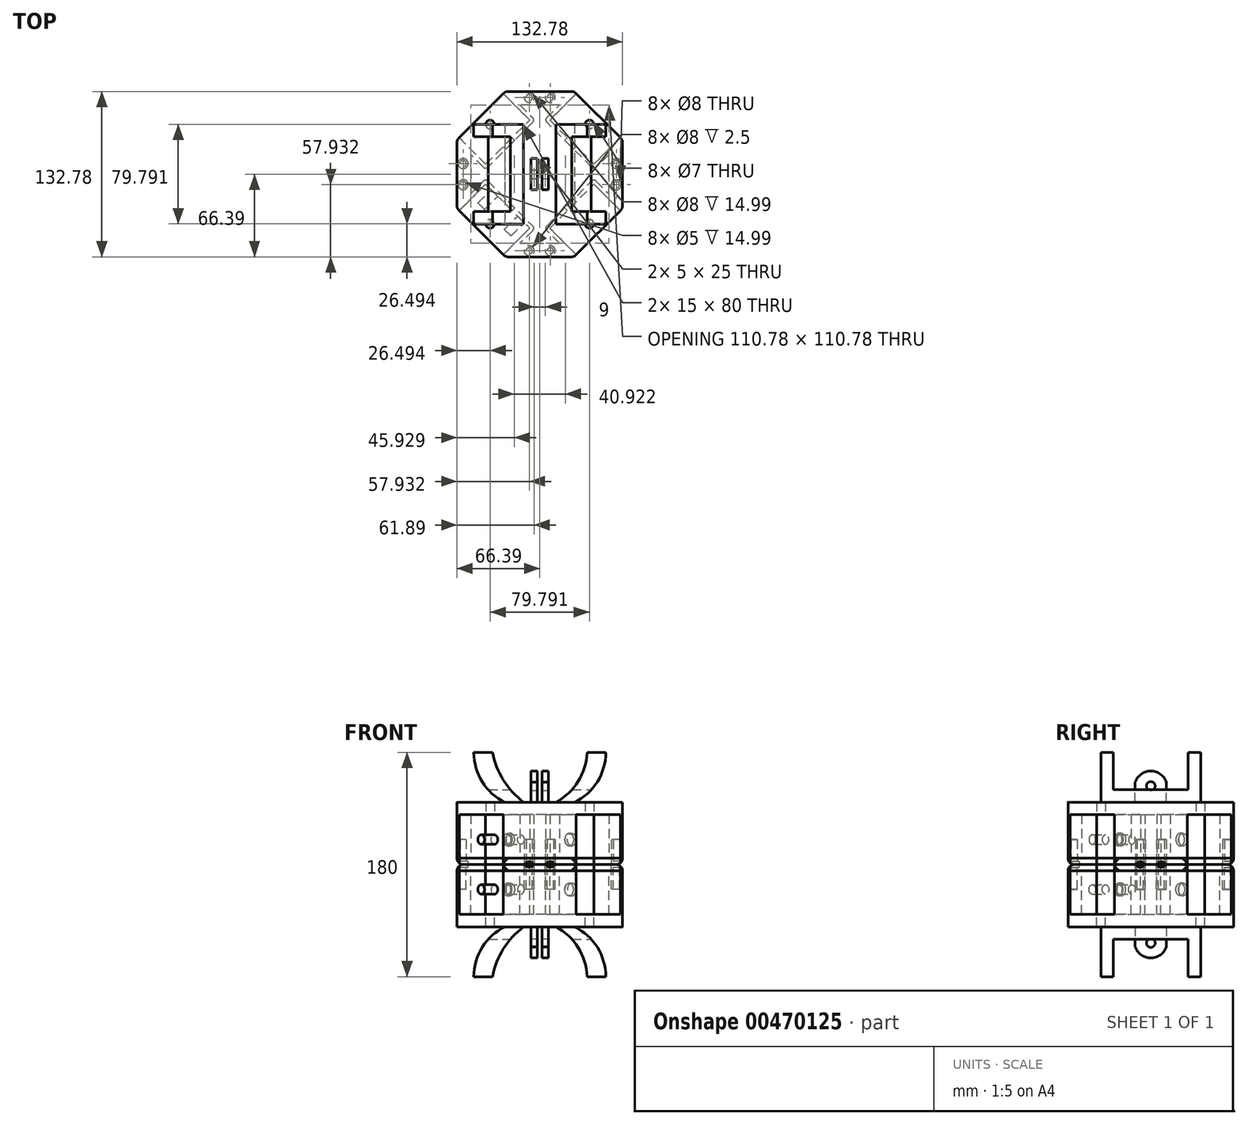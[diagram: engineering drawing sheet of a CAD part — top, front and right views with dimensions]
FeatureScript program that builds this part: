
annotation { "Feature Type Name" : "Feature", "Feature Type Description" : "" }
export const myFeature = defineFeature(function(context is Context, id is Id, definition is map)
    precondition{}
    {
        {
            var Q0;
            Q0=qCreatedBy(makeId("Top.planeOp"),FACE);
            var sketch = newSketch(context, id + "F0", { "sketchPlane" : qUnion([Q0])});
            skCircle(sketch, "E0.cCircle", {"center": v(0, 0) * mm, "radius": 71.86 * mm, "construction": true});
            skLineSegment(sketch, "E0.0", {"start": v(66.4, 27.5) * mm, "end": v(66.4, -27.5) * mm});
            skLineSegment(sketch, "E0.1", {"start": v(66.4, -27.5) * mm, "end": v(27.5, -66.4) * mm});
            skLineSegment(sketch, "E0.2", {"start": v(27.5, -66.4) * mm, "end": v(-27.5, -66.4) * mm});
            skLineSegment(sketch, "E0.3", {"start": v(-27.5, -66.4) * mm, "end": v(-66.4, -27.5) * mm});
            skLineSegment(sketch, "E0.4", {"start": v(-66.4, -27.5) * mm, "end": v(-66.4, 27.5) * mm});
            skLineSegment(sketch, "E0.5", {"start": v(-66.4, 27.5) * mm, "end": v(-27.5, 66.4) * mm});
            skLineSegment(sketch, "E0.6", {"start": v(-27.5, 66.4) * mm, "end": v(27.5, 66.4) * mm});
            skLineSegment(sketch, "E0.7", {"start": v(27.5, 66.4) * mm, "end": v(66.4, 27.5) * mm});
            skSolve(sketch);
        }
        {
            var Q0;
            Q0=makeQuery(id+"F0.imprint","IMPRINT",FACE,{"disambiguationData":[TD([[makeQuery(id+"F0.imprint","IMPRINT",EDGE,{"derivedFrom":sQuery(id+"F0.wireOp",EDGE,"E0.0")}),-1.0]])]});
            extrude(context, id + "F1", {"entities" : qUnion([Q0]), "depth" : 50 * mm});
        }
        {
            var Q0;
            Q0=makeQuery(id+"F1.opExtrude","CAP_FACE",FACE,{"disambiguationData":[OSD([sQuery(id+"F0.wireOp",EDGE,"E0.0"),sQuery(id+"F0.wireOp",EDGE,"E0.1"),sQuery(id+"F0.wireOp",EDGE,"E0.2"),sQuery(id+"F0.wireOp",EDGE,"E0.3"),sQuery(id+"F0.wireOp",EDGE,"E0.4"),sQuery(id+"F0.wireOp",EDGE,"E0.5"),sQuery(id+"F0.wireOp",EDGE,"E0.6"),sQuery(id+"F0.wireOp",EDGE,"E0.7")])],"isStart":true});
            var sketch = newSketch(context, id + "F2", { "sketchPlane" : qUnion([Q0])});
            skLineSegment(sketch, "E1", {"start": v(0, 66.4) * mm, "end": v(0, -66.4) * mm});
            skLineSegment(sketch, "E2.bottom", {"start": v(52.96, 40) * mm, "end": v(12.96, 40) * mm});
            skLineSegment(sketch, "E2.top", {"start": v(52.96, -40) * mm, "end": v(12.96, -40) * mm});
            skLineSegment(sketch, "E2.left", {"start": v(52.96, 40) * mm, "end": v(52.96, -40) * mm});
            skLineSegment(sketch, "E2.right", {"start": v(12.96, 40) * mm, "end": v(12.96, -40) * mm});
            skPoint(sketch, "E2.middle", {"position": v(32.96, 0) * mm});
            skLineSegment(sketch, "E3.MirrorCS", {"start": v(-12.96, 40) * mm, "end": v(-12.96, -40) * mm});
            skLineSegment(sketch, "E4.MirrorCS", {"start": v(-52.96, 40) * mm, "end": v(-12.96, 40) * mm});
            skLineSegment(sketch, "E5.MirrorCS", {"start": v(-52.96, 40) * mm, "end": v(-52.96, -40) * mm});
            skLineSegment(sketch, "E6.MirrorCS", {"start": v(-52.96, -40) * mm, "end": v(-12.96, -40) * mm});
            skSolve(sketch);
        }
        {
            var Q0;
            Q0 = qSketchRegion(id + "F2", true);
            extrude(context, id + "F3", {"entities" : qUnion([Q0]), "operationType" : NewBodyOperationType.ADD, "depth" : 40 * mm});
        }
        {
            var Q0;
            Q0=makeQuery(id+"F3.opExtrude","SWEPT_FACE",FACE,{"disambiguationData":[OSD([sQuery(id+"F2.wireOp",EDGE,"E2.bottom")])]});
            var sketch = newSketch(context, id + "F4", { "sketchPlane" : qUnion([Q0])});
            skArc(sketch, "E7", {"start": v(52.96, -40) * mm, "mid": v(46.2, -16.42) * mm, "end": v(27.96, 0) * mm});
            skArc(sketch, "E8", {"start": v(37.96, -40) * mm, "mid": v(30.79, -16.67) * mm, "end": v(12.96, 0) * mm});
            skLineSegment(sketch, "E9", {"start": v(0, 0) * mm, "end": v(0, -51.15) * mm});
            skArc(sketch, "E10.MirrorCS", {"start": v(-37.96, -40) * mm, "mid": v(-30.79, -16.67) * mm, "end": v(-12.96, 0) * mm});
            skArc(sketch, "E11.MirrorCS", {"start": v(-52.96, -40) * mm, "mid": v(-46.2, -16.42) * mm, "end": v(-27.96, 0) * mm});
            skLineSegment(sketch, "E12", {"start": v(-37.96, -40) * mm, "end": v(-52.96, -40) * mm});
            skLineSegment(sketch, "E13", {"start": v(-27.96, 0) * mm, "end": v(-12.96, 0) * mm});
            skSolve(sketch);
        }
        {
            var Q0;
            {var subQ0=sQuery(id+"F4.wireOp",EDGE,"E7");Q0=makeQuery(id+"F4.imprint","IMPRINT",FACE,{"disambiguationData":[TD([[makeQuery(id+"F4.imprint","IMPRINT",EDGE,{"derivedFrom":subQ0}),-1.0]])]});}
            var Q1;
            {var subQ0=sQuery(id+"F4.wireOp",EDGE,"E8");Q1=makeQuery(id+"F4.imprint","IMPRINT",FACE,{"disambiguationData":[TD([[makeQuery(id+"F4.imprint","IMPRINT",EDGE,{"derivedFrom":subQ0}),1.0]])]});}
            extrude(context, id + "F5", {"entities" : qUnion([Q0, Q1]), "operationType" : NewBodyOperationType.REMOVE, "endBound" : BoundingType.THROUGH_ALL, "oppositeDirection" : true, "depth" : 25 * mm});
        }
        {
            var Q0;
            Q0=makeQuery(id+"F3.opExtrude","SWEPT_FACE",FACE,{"disambiguationData":[OSD([sQuery(id+"F2.wireOp",EDGE,"E4.MirrorCS")])]});
            var sketch = newSketch(context, id + "F6", { "sketchPlane" : qUnion([Q0])});
            skArc(sketch, "E14", {"start": v(-27.96, 0) * mm, "mid": v(-46.2, -16.42) * mm, "end": v(-52.96, -40) * mm});
            skArc(sketch, "E15", {"start": v(-12.96, 0) * mm, "mid": v(-29.15, -17.7) * mm, "end": v(-37.96, -40) * mm});
            skSolve(sketch);
        }
        {
            var Q0;
            {var subQ0=sQuery(id+"F6.wireOp",EDGE,"E15");Q0=makeQuery(id+"F6.imprint","IMPRINT",FACE,{"disambiguationData":[TD([[makeQuery(id+"F6.imprint","IMPRINT",EDGE,{"derivedFrom":subQ0}),1.0]])]});}
            var Q1;
            {var subQ0=sQuery(id+"F6.wireOp",EDGE,"E14");Q1=makeQuery(id+"F6.imprint","IMPRINT",FACE,{"disambiguationData":[TD([[makeQuery(id+"F6.imprint","IMPRINT",EDGE,{"derivedFrom":subQ0}),-1.0]])]});}
            extrude(context, id + "F7", {"entities" : qUnion([Q0, Q1]), "operationType" : NewBodyOperationType.REMOVE, "endBound" : BoundingType.THROUGH_ALL, "oppositeDirection" : true, "depth" : 25 * mm});
        }
        {
            var Q0;
            Q0=makeQuery(id+"F3.opExtrude","CAP_FACE",FACE,{"disambiguationData":[OSD([sQuery(id+"F2.wireOp",EDGE,"E2.bottom"),sQuery(id+"F2.wireOp",EDGE,"E2.top"),sQuery(id+"F2.wireOp",EDGE,"E2.left"),sQuery(id+"F2.wireOp",EDGE,"E2.right")])],"isStart":false});
            extrude(context, id + "F8", {"entities" : qUnion([Q0]), "operationType" : NewBodyOperationType.ADD, "depth" : 10 * mm});
        }
        {
            var Q0;
            Q0=makeQuery(id+"F8.opExtrude","SWEPT_FACE",FACE,{"disambiguationData":[OSD([sQuery(id+"F2.wireOp",EDGE,"E2.bottom"),sQuery(id+"F2.wireOp",EDGE,"E2.left"),sQuery(id+"F4.wireOp",EDGE,"E7")])]});
            var sketch = newSketch(context, id + "F9", { "sketchPlane" : qUnion([Q0])});
            skLineSegment(sketch, "E16.bottom", {"start": v(-30, -50) * mm, "end": v(30, -50) * mm});
            skLineSegment(sketch, "E16.top", {"start": v(-30, -10) * mm, "end": v(30, -10) * mm});
            skLineSegment(sketch, "E16.left", {"start": v(-30, -50) * mm, "end": v(-30, -10) * mm});
            skLineSegment(sketch, "E16.right", {"start": v(30, -50) * mm, "end": v(30, -10) * mm});
            skLineSegment(sketch, "E17.bottom", {"start": v(-40, -40) * mm, "end": v(40, -40) * mm});
            skLineSegment(sketch, "E17.top", {"start": v(-40, -50) * mm, "end": v(40, -50) * mm});
            skLineSegment(sketch, "E17.left", {"start": v(-40, -40) * mm, "end": v(-40, -50) * mm});
            skLineSegment(sketch, "E17.right", {"start": v(40, -40) * mm, "end": v(40, -50) * mm});
            skSolve(sketch);
        }
        {
            var Q0;
            Q0 = qSketchRegion(id + "F9", true);
            extrude(context, id + "F10", {"entities" : qUnion([Q0]), "operationType" : NewBodyOperationType.REMOVE, "endBound" : BoundingType.THROUGH_ALL, "oppositeDirection" : true, "depth" : 25 * mm});
        }
        {
            var Q0;
            Q0=makeQuery(id+"F1.opExtrude","CAP_FACE",FACE,{"disambiguationData":[OSD([sQuery(id+"F0.wireOp",EDGE,"E0.0"),sQuery(id+"F0.wireOp",EDGE,"E0.1"),sQuery(id+"F0.wireOp",EDGE,"E0.2"),sQuery(id+"F0.wireOp",EDGE,"E0.3"),sQuery(id+"F0.wireOp",EDGE,"E0.4"),sQuery(id+"F0.wireOp",EDGE,"E0.5"),sQuery(id+"F0.wireOp",EDGE,"E0.6"),sQuery(id+"F0.wireOp",EDGE,"E0.7")])],"isStart":false});
            var sketch = newSketch(context, id + "F11", { "sketchPlane" : qUnion([Q0])});
            skLineSegment(sketch, "E18", {"start": v(29.27, -64.62) * mm, "end": v(8.05, -43.4) * mm});
            skLineSegment(sketch, "E19", {"start": v(64.62, -29.27) * mm, "end": v(43.4, -8.05) * mm});
            skLineSegment(sketch, "E20", {"start": v(8.05, -43.4) * mm, "end": v(43.4, -8.05) * mm});
            skLineSegment(sketch, "E21", {"start": v(43.4, 43.4) * mm, "end": v(-46.95, -46.95) * mm});
            skLineSegment(sketch, "E22", {"start": v(46.95, -46.95) * mm, "end": v(-46.95, 46.95) * mm});
            skLineSegment(sketch, "E23", {"start": v(-29.27, -64.62) * mm, "end": v(-8.05, -43.4) * mm});
            skLineSegment(sketch, "E24", {"start": v(-64.62, -29.27) * mm, "end": v(-43.4, -8.05) * mm});
            skLineSegment(sketch, "E25", {"start": v(-43.4, -8.05) * mm, "end": v(-8.05, -43.4) * mm});
            skLineSegment(sketch, "E26.MirrorCS", {"start": v(29.27, 64.62) * mm, "end": v(8.05, 43.4) * mm});
            skLineSegment(sketch, "E27.MirrorCS", {"start": v(8.05, 43.4) * mm, "end": v(43.4, 8.05) * mm});
            skLineSegment(sketch, "E28.MirrorCS", {"start": v(64.62, 29.27) * mm, "end": v(43.4, 8.05) * mm});
            skLineSegment(sketch, "E29.MirrorCS", {"start": v(-43.4, 8.05) * mm, "end": v(-8.05, 43.4) * mm});
            skLineSegment(sketch, "E30.MirrorCS", {"start": v(-29.27, 64.62) * mm, "end": v(-8.05, 43.4) * mm});
            skLineSegment(sketch, "E31", {"start": v(-43.4, 8.05) * mm, "end": v(-64.62, 29.27) * mm});
            skSolve(sketch);
        }
        {
            var Q0;
            {var subQ5=sQuery(id+"F11.wireOp",EDGE,"0e1623ae-2a34-4fe9-b9fa-2a8e952514210.MirrorCS");Q0=makeQuery(id+"F11.imprint","IMPRINT",FACE,{"disambiguationData":[TD([[makeQuery(id+"F11.imprint","IMPRINT",EDGE,{"derivedFrom":subQ5}),1.0]])]});}
            var Q1;
            {var subQ5=sQuery(id+"F11.wireOp",EDGE,"E30.MirrorCS");Q1=makeQuery(id+"F11.imprint","IMPRINT",FACE,{"disambiguationData":[TD([[makeQuery(id+"F11.imprint","IMPRINT",EDGE,{"derivedFrom":subQ5}),-1.0]])]});}
            var Q2;
            {var subQ5=sQuery(id+"F11.wireOp",EDGE,"E26.MirrorCS");Q2=makeQuery(id+"F11.imprint","IMPRINT",FACE,{"disambiguationData":[TD([[makeQuery(id+"F11.imprint","IMPRINT",EDGE,{"derivedFrom":subQ5}),1.0]])]});}
            var Q3;
            {var subQ5=sQuery(id+"F11.wireOp",EDGE,"E28.MirrorCS");Q3=makeQuery(id+"F11.imprint","IMPRINT",FACE,{"disambiguationData":[TD([[makeQuery(id+"F11.imprint","IMPRINT",EDGE,{"derivedFrom":subQ5}),-1.0]])]});}
            var Q4;
            {var subQ0=sQuery(id+"F11.wireOp",EDGE,"E19");Q4=makeQuery(id+"F11.imprint","IMPRINT",FACE,{"disambiguationData":[TD([[makeQuery(id+"F11.imprint","IMPRINT",EDGE,{"derivedFrom":subQ0}),1.0]])]});}
            var Q5;
            {var subQ0=sQuery(id+"F11.wireOp",EDGE,"E18");Q5=makeQuery(id+"F11.imprint","IMPRINT",FACE,{"disambiguationData":[TD([[makeQuery(id+"F11.imprint","IMPRINT",EDGE,{"derivedFrom":subQ0}),-1.0]])]});}
            var Q6;
            {var subQ5=sQuery(id+"F11.wireOp",EDGE,"E24");Q6=makeQuery(id+"F11.imprint","IMPRINT",FACE,{"disambiguationData":[TD([[makeQuery(id+"F11.imprint","IMPRINT",EDGE,{"derivedFrom":subQ5}),-1.0]])]});}
            var Q7;
            {var subQ5=sQuery(id+"F11.wireOp",EDGE,"E23");Q7=makeQuery(id+"F11.imprint","IMPRINT",FACE,{"disambiguationData":[TD([[makeQuery(id+"F11.imprint","IMPRINT",EDGE,{"derivedFrom":subQ5}),1.0]])]});}
            var Q8;
            {var subQ5=sQuery(id+"F11.wireOp",EDGE,"E31");Q8=makeQuery(id+"F11.imprint","IMPRINT",FACE,{"disambiguationData":[TD([[makeQuery(id+"F11.imprint","IMPRINT",EDGE,{"derivedFrom":subQ5}),-1.0]])]});}
            extrude(context, id + "F12", {"entities" : qUnion([Q0, Q1, Q2, Q3, Q4, Q5, Q6, Q7, Q8]), "operationType" : NewBodyOperationType.REMOVE, "oppositeDirection" : true, "depth" : 40 * mm});
        }
        {
            var Q0;
            {var subQ0=sQuery(id+"F2.wireOp",EDGE,"E4.MirrorCS");var subQ1=makeQuery(id+"F3.opExtrude","CAP_EDGE",EDGE,{"disambiguationData":[OSD([subQ0])],"isStart":true});var subQ2=sQuery(id+"F2.wireOp",EDGE,"E2.bottom");var subQ3=makeQuery(id+"F3.opExtrude","CAP_EDGE",EDGE,{"disambiguationData":[OSD([subQ2])],"isStart":true});Q0=makeQuery(id+"F7.boolean.opBoolean","MERGE",FACE,{"derivedFrom":[makeQuery(id+"F5.boolean.opBoolean","MERGE",FACE,{"derivedFrom":[makeQuery(id+"F1.opExtrude","CAP_FACE",FACE,{"disambiguationData":[OSD([sQuery(id+"F0.wireOp",EDGE,"E0.0"),sQuery(id+"F0.wireOp",EDGE,"E0.1"),sQuery(id+"F0.wireOp",EDGE,"E0.2"),sQuery(id+"F0.wireOp",EDGE,"E0.3"),sQuery(id+"F0.wireOp",EDGE,"E0.4"),sQuery(id+"F0.wireOp",EDGE,"E0.5"),sQuery(id+"F0.wireOp",EDGE,"E0.6"),sQuery(id+"F0.wireOp",EDGE,"E0.7")])],"isStart":true}),makeQuery(id+"F5.opExtrude","SWEPT_FACE",FACE,{"disambiguationData":[OSD([subQ2]),TDD([makeQuery(id+"F4.imprint","IMPRINT",EDGE,{"disambiguationData":[TD([[makeQuery(id+"F4.imprint","INTERSECT",VERTEX,{"derivedFrom":[subQ3,sQuery(id+"F4.wireOp",EDGE,"E7")]}),1.0]])],"derivedFrom":subQ3})])]})]}),makeQuery(id+"F7.opExtrude","SWEPT_FACE",FACE,{"disambiguationData":[OSD([subQ0]),TDD([makeQuery(id+"F6.imprint","IMPRINT",EDGE,{"disambiguationData":[TD([[makeQuery(id+"F6.imprint","INTERSECT",VERTEX,{"derivedFrom":[subQ1,sQuery(id+"F6.wireOp",EDGE,"E14")]}),1.0]])],"derivedFrom":subQ1})])]})]});}
            var sketch = newSketch(context, id + "F13", { "sketchPlane" : qUnion([Q0])});
            skLineSegment(sketch, "E32.bottom", {"start": v(10, 12.5) * mm, "end": v(-10, 12.5) * mm});
            skLineSegment(sketch, "E32.top", {"start": v(10, -12.5) * mm, "end": v(-10, -12.5) * mm});
            skLineSegment(sketch, "E32.left", {"start": v(10, 12.5) * mm, "end": v(10, -12.5) * mm});
            skLineSegment(sketch, "E32.right", {"start": v(-10, 12.5) * mm, "end": v(-10, -12.5) * mm});
            skPoint(sketch, "E32.middle", {"position": v(0, 0) * mm});
            skSolve(sketch);
        }
        {
            var Q0;
            Q0 = qSketchRegion(id + "F13", true);
            extrude(context, id + "F14", {"entities" : qUnion([Q0]), "operationType" : NewBodyOperationType.ADD, "depth" : 25 * mm});
        }
        {
            var Q0;
            Q0=makeQuery(id+"F14.opExtrude","CAP_FACE",FACE,{"disambiguationData":[OSD([sQuery(id+"F13.wireOp",EDGE,"E32.bottom"),sQuery(id+"F13.wireOp",EDGE,"E32.top"),sQuery(id+"F13.wireOp",EDGE,"E32.left"),sQuery(id+"F13.wireOp",EDGE,"E32.right")])],"isStart":false});
            var sketch = newSketch(context, id + "F15", { "sketchPlane" : qUnion([Q0])});
            skLineSegment(sketch, "E33.bottom", {"start": v(-7, 12.5) * mm, "end": v(-2, 12.5) * mm});
            skLineSegment(sketch, "E33.top", {"start": v(-7, -12.5) * mm, "end": v(-2, -12.5) * mm});
            skLineSegment(sketch, "E33.left", {"start": v(-7, 12.5) * mm, "end": v(-7, -12.5) * mm});
            skLineSegment(sketch, "E33.right", {"start": v(-2, 12.5) * mm, "end": v(-2, -12.5) * mm});
            skLineSegment(sketch, "E34.bottom", {"start": v(7, 12.5) * mm, "end": v(2, 12.5) * mm});
            skLineSegment(sketch, "E34.top", {"start": v(7, -12.5) * mm, "end": v(2, -12.5) * mm});
            skLineSegment(sketch, "E34.left", {"start": v(7, 12.5) * mm, "end": v(7, -12.5) * mm});
            skLineSegment(sketch, "E34.right", {"start": v(2, 12.5) * mm, "end": v(2, -12.5) * mm});
            skSolve(sketch);
        }
        {
            var Q0;
            Q0=makeQuery(id+"F14.opExtrude","SWEPT_FACE",FACE,{"disambiguationData":[OSD([sQuery(id+"F13.wireOp",EDGE,"E32.left")])]});
            var sketch = newSketch(context, id + "F16", { "sketchPlane" : qUnion([Q0])});
            skPoint(sketch, "E35", {"position": v(0, -25) * mm});
            skPoint(sketch, "E36", {"position": v(12.5, -16.09) * mm});
            skPoint(sketch, "E37", {"position": v(-12.5, -16.09) * mm});
            skArc(sketch, "E38", {"start": v(-12.5, -16.09) * mm, "mid": v(0, -25) * mm, "end": v(12.5, -16.09) * mm});
            skCircle(sketch, "E39", {"center": v(0, -13) * mm, "radius": 3.5 * mm});
            skSolve(sketch);
        }
        {
            var Q0;
            {var subQ0=sQuery(id+"F16.wireOp",EDGE,"E38");var subQ1=sQuery(id+"F13.wireOp",EDGE,"E32.left");var subQ4=makeQuery(id+"F14.opExtrude","CAP_EDGE",EDGE,{"disambiguationData":[OSD([subQ1])],"isStart":false});var subQ5=makeQuery(id+"F16.imprint","INTERSECT",VERTEX,{"derivedFrom":[subQ4,subQ0]});Q0=makeQuery(id+"F16.imprint","IMPRINT",FACE,{"disambiguationData":[TD([[makeQuery(id+"F16.imprint","IMPRINT",EDGE,{"disambiguationData":[TD([[subQ5,-1.0]])],"derivedFrom":subQ0}),-1.0]])]});}
            var Q1;
            {var subQ0=sQuery(id+"F16.wireOp",EDGE,"E38");var subQ1=sQuery(id+"F13.wireOp",EDGE,"E32.left");var subQ4=makeQuery(id+"F14.opExtrude","CAP_EDGE",EDGE,{"disambiguationData":[OSD([subQ1])],"isStart":false});var subQ5=makeQuery(id+"F16.imprint","INTERSECT",VERTEX,{"derivedFrom":[subQ4,subQ0]});Q1=makeQuery(id+"F16.imprint","IMPRINT",FACE,{"disambiguationData":[TD([[makeQuery(id+"F16.imprint","IMPRINT",EDGE,{"disambiguationData":[TD([[subQ5,1.0]])],"derivedFrom":subQ0}),-1.0]])]});}
            extrude(context, id + "F17", {"entities" : qUnion([Q0, Q1]), "operationType" : NewBodyOperationType.REMOVE, "endBound" : BoundingType.THROUGH_ALL, "oppositeDirection" : true, "depth" : 25 * mm});
        }
        {
            var Q0;
            {var subQ0=sQuery(id+"F15.wireOp",EDGE,"E34.left");Q0=makeQuery(id+"F15.imprint","IMPRINT",FACE,{"disambiguationData":[TD([[makeQuery(id+"F15.imprint","IMPRINT",EDGE,{"derivedFrom":subQ0}),1.0]])]});}
            var Q1;
            {var subQ0=sQuery(id+"F15.wireOp",EDGE,"E33.right");Q1=makeQuery(id+"F15.imprint","IMPRINT",FACE,{"disambiguationData":[TD([[makeQuery(id+"F15.imprint","IMPRINT",EDGE,{"derivedFrom":subQ0}),1.0]])]});}
            var Q2;
            {var subQ0=sQuery(id+"F15.wireOp",EDGE,"E33.left");Q2=makeQuery(id+"F15.imprint","IMPRINT",FACE,{"disambiguationData":[TD([[makeQuery(id+"F15.imprint","IMPRINT",EDGE,{"derivedFrom":subQ0}),-1.0]])]});}
            extrude(context, id + "F18", {"entities" : qUnion([Q0, Q1, Q2]), "operationType" : NewBodyOperationType.REMOVE, "oppositeDirection" : true, "depth" : 25 * mm});
        }
        {
            var Q0;
            Q0=makeQuery(id+"F12.boolean.opBoolean","COPY",FACE,{"derivedFrom":makeQuery(id+"F12.opExtrude","CAP_FACE",FACE,{"disambiguationData":[OSD([sQuery(id+"F0.wireOp",EDGE,"E0.1"),sQuery(id+"F11.wireOp",EDGE,"E18"),sQuery(id+"F11.wireOp",EDGE,"E19"),sQuery(id+"F11.wireOp",EDGE,"E20")])],"isStart":false})});
            var sketch = newSketch(context, id + "F19", { "sketchPlane" : qUnion([Q0])});
            skCircle(sketch, "E40", {"center": v(39.9, -39.85) * mm, "radius": 3.5 * mm});
            skSolve(sketch);
        }
        {
            var Q0;
            Q0 = qSketchRegion(id + "F16", true);
            extrude(context, id + "F20", {"entities" : qUnion([Q0]), "operationType" : NewBodyOperationType.REMOVE, "oppositeDirection" : true, "depth" : 25 * mm});
        }
        {
            var Q0;
            Q0=makeQuery(id+"F12.boolean.opBoolean","COPY",FACE,{"derivedFrom":makeQuery(id+"F12.opExtrude","CAP_FACE",FACE,{"disambiguationData":[OSD([sQuery(id+"F0.wireOp",EDGE,"E0.3"),sQuery(id+"F11.wireOp",EDGE,"E23"),sQuery(id+"F11.wireOp",EDGE,"E24"),sQuery(id+"F11.wireOp",EDGE,"E25")])],"isStart":false})});
            var sketch = newSketch(context, id + "F21", { "sketchPlane" : qUnion([Q0])});
            skCircle(sketch, "E41", {"center": v(-39.85, -39.9) * mm, "radius": 3.5 * mm});
            skSolve(sketch);
        }
        {
            var Q0;
            Q0=makeQuery(id+"F12.boolean.opBoolean","COPY",FACE,{"derivedFrom":makeQuery(id+"F12.opExtrude","CAP_FACE",FACE,{"disambiguationData":[OSD([sQuery(id+"F0.wireOp",EDGE,"E0.5"),sQuery(id+"F11.wireOp",EDGE,"E29.MirrorCS"),sQuery(id+"F11.wireOp",EDGE,"0e1623ae-2a34-4fe9-b9fa-2a8e952514210.MirrorCS"),sQuery(id+"F11.wireOp",EDGE,"E30.MirrorCS")])],"isStart":false})});
            var sketch = newSketch(context, id + "F22", { "sketchPlane" : qUnion([Q0])});
            skCircle(sketch, "E42", {"center": v(-39.9, 39.85) * mm, "radius": 3.5 * mm});
            skSolve(sketch);
        }
        {
            var Q0;
            Q0=makeQuery(id+"F12.boolean.opBoolean","COPY",FACE,{"derivedFrom":makeQuery(id+"F12.opExtrude","CAP_FACE",FACE,{"disambiguationData":[OSD([sQuery(id+"F0.wireOp",EDGE,"E0.7"),sQuery(id+"F11.wireOp",EDGE,"E26.MirrorCS"),sQuery(id+"F11.wireOp",EDGE,"E27.MirrorCS"),sQuery(id+"F11.wireOp",EDGE,"E28.MirrorCS")])],"isStart":false})});
            var sketch = newSketch(context, id + "F23", { "sketchPlane" : qUnion([Q0])});
            skCircle(sketch, "E43", {"center": v(39.85, 39.9) * mm, "radius": 3.5 * mm});
            skSolve(sketch);
        }
        {
            var Q0;
            Q0=makeQuery(id+"F22.imprint","IMPRINT",FACE,{"disambiguationData":[TD([[makeQuery(id+"F22.imprint","IMPRINT",EDGE,{"derivedFrom":sQuery(id+"F22.wireOp",EDGE,"E42")}),1.0]])]});
            var Q1;
            Q1=makeQuery(id+"F23.imprint","IMPRINT",FACE,{"disambiguationData":[TD([[makeQuery(id+"F23.imprint","IMPRINT",EDGE,{"derivedFrom":sQuery(id+"F23.wireOp",EDGE,"E43")}),1.0]])]});
            var Q2;
            Q2=makeQuery(id+"F19.imprint","IMPRINT",FACE,{"disambiguationData":[TD([[makeQuery(id+"F19.imprint","IMPRINT",EDGE,{"derivedFrom":sQuery(id+"F19.wireOp",EDGE,"E40")}),1.0]])]});
            var Q3;
            Q3=makeQuery(id+"F21.imprint","IMPRINT",FACE,{"disambiguationData":[TD([[makeQuery(id+"F21.imprint","IMPRINT",EDGE,{"derivedFrom":sQuery(id+"F21.wireOp",EDGE,"E41")}),1.0]])]});
            extrude(context, id + "F24", {"entities" : qUnion([Q0, Q1, Q2, Q3]), "operationType" : NewBodyOperationType.REMOVE, "oppositeDirection" : true, "depth" : 10 * mm});
        }
        {
            var Q0;
            Q0=makeQuery(id+"F1.opExtrude","CAP_EDGE",EDGE,{"disambiguationData":[OSD([sQuery(id+"F0.wireOp",EDGE,"E0.2")])],"isStart":false});
            var Q1;
            Q1=makeQuery(id+"F1.opExtrude","CAP_EDGE",EDGE,{"disambiguationData":[OSD([sQuery(id+"F0.wireOp",EDGE,"E0.0")])],"isStart":false});
            var Q2;
            Q2=makeQuery(id+"F1.opExtrude","CAP_EDGE",EDGE,{"disambiguationData":[OSD([sQuery(id+"F0.wireOp",EDGE,"E0.6")])],"isStart":false});
            var Q3;
            Q3=makeQuery(id+"F1.opExtrude","CAP_EDGE",EDGE,{"disambiguationData":[OSD([sQuery(id+"F0.wireOp",EDGE,"E0.4")])],"isStart":false});
            var Q4;
            Q4=makeQuery(id+"F1.opExtrude","SWEPT_EDGE",EDGE,{"disambiguationData":[OSD([sQuery(id+"F0.wireOp",EDGE,"E0.1"),sQuery(id+"F0.wireOp",EDGE,"E0.2")])]});
            var Q5;
            Q5=makeQuery(id+"F1.opExtrude","SWEPT_EDGE",EDGE,{"disambiguationData":[OSD([sQuery(id+"F0.wireOp",EDGE,"E0.2"),sQuery(id+"F0.wireOp",EDGE,"E0.3")])]});
            var Q6;
            Q6=makeQuery(id+"F1.opExtrude","SWEPT_EDGE",EDGE,{"disambiguationData":[OSD([sQuery(id+"F0.wireOp",EDGE,"E0.0"),sQuery(id+"F0.wireOp",EDGE,"E0.1")])]});
            var Q7;
            Q7=makeQuery(id+"F1.opExtrude","SWEPT_EDGE",EDGE,{"disambiguationData":[OSD([sQuery(id+"F0.wireOp",EDGE,"E0.0"),sQuery(id+"F0.wireOp",EDGE,"E0.7")])]});
            var Q8;
            Q8=makeQuery(id+"F1.opExtrude","SWEPT_EDGE",EDGE,{"disambiguationData":[OSD([sQuery(id+"F0.wireOp",EDGE,"E0.6"),sQuery(id+"F0.wireOp",EDGE,"E0.7")])]});
            var Q9;
            Q9=makeQuery(id+"F1.opExtrude","SWEPT_EDGE",EDGE,{"disambiguationData":[OSD([sQuery(id+"F0.wireOp",EDGE,"E0.4"),sQuery(id+"F0.wireOp",EDGE,"E0.5")])]});
            var Q10;
            Q10=makeQuery(id+"F1.opExtrude","SWEPT_EDGE",EDGE,{"disambiguationData":[OSD([sQuery(id+"F0.wireOp",EDGE,"E0.3"),sQuery(id+"F0.wireOp",EDGE,"E0.4")])]});
            var Q11;
            Q11=makeQuery(id+"F1.opExtrude","SWEPT_EDGE",EDGE,{"disambiguationData":[OSD([sQuery(id+"F0.wireOp",EDGE,"E0.5"),sQuery(id+"F0.wireOp",EDGE,"E0.6")])]});
            fillet(context, id + "F25", {"entities" : qUnion([Q0, Q1, Q2, Q3, Q4, Q5, Q6, Q7, Q8, Q9, Q10, Q11]), "radius" : 5 * mm, "tangentPropagation" : true, "allowEdgeOverflow" : false});
        }
        {
            var Q0;
            Q0=makeQuery(id+"F1.opExtrude","SWEPT_FACE",FACE,{"disambiguationData":[OSD([sQuery(id+"F0.wireOp",EDGE,"E0.2")])]});
            var sketch = newSketch(context, id + "F26", { "sketchPlane" : qUnion([Q0])});
            skLineSegment(sketch, "E44.bottom", {"start": v(90.93, 45) * mm, "end": v(-90.93, 45) * mm});
            skLineSegment(sketch, "E44.top", {"start": v(90.93, 44.99) * mm, "end": v(-90.93, 44.99) * mm});
            skLineSegment(sketch, "E44.left", {"start": v(90.93, 45) * mm, "end": v(90.93, 44.99) * mm});
            skLineSegment(sketch, "E44.right", {"start": v(-90.93, 45) * mm, "end": v(-90.93, 44.99) * mm});
            skPoint(sketch, "E44.middle", {"position": v(0, 45) * mm});
            skPoint(sketch, "E44.middle.positionSnap0", {"position": v(0, 45) * mm});
            skPoint(sketch, "E44.cornerSnap0", {"position": v(0, 45) * mm});
            skPoint(sketch, "E44.centerSnap0", {"position": v(0, 45) * mm});
            skSolve(sketch);
        }
        {
            var Q0;
            Q0 = qSketchRegion(id + "F26", true);
            extrude(context, id + "F27", {"entities" : qUnion([Q0]), "operationType" : NewBodyOperationType.REMOVE, "endBound" : BoundingType.THROUGH_ALL, "oppositeDirection" : true, "depth" : 25 * mm});
        }
        {
            var Q0;
            Q0=makeQuery(id+"F27.boolean.opBoolean","COPY",FACE,{"derivedFrom":makeQuery(id+"F27.opExtrude","SWEPT_FACE",FACE,{"disambiguationData":[OSD([sQuery(id+"F26.wireOp",EDGE,"E44.top")])]})});
            var sketch = newSketch(context, id + "F28", { "sketchPlane" : qUnion([Q0])});
            skLineSegment(sketch, "E45.0", {"start": v(-3.81, -43.4) * mm, "end": v(-23.8, -63.4) * mm});
            skLineSegment(sketch, "E45.1", {"start": v(-43.4, -3.81) * mm, "end": v(-3.81, -43.4) * mm});
            skLineSegment(sketch, "E45.2", {"start": v(-63.4, -23.8) * mm, "end": v(-43.4, -3.81) * mm});
            skLineSegment(sketch, "E45.3", {"start": v(-63.4, 23.8) * mm, "end": v(-63.4, -23.8) * mm});
            skLineSegment(sketch, "E45.4", {"start": v(-43.4, 3.81) * mm, "end": v(-63.4, 23.8) * mm});
            skLineSegment(sketch, "E45.5", {"start": v(63.4, -23.8) * mm, "end": v(63.4, 23.8) * mm});
            skLineSegment(sketch, "E45.6", {"start": v(43.4, -3.81) * mm, "end": v(63.4, -23.8) * mm});
            skLineSegment(sketch, "E45.7", {"start": v(3.81, -43.4) * mm, "end": v(43.4, -3.81) * mm});
            skLineSegment(sketch, "E45.8", {"start": v(23.8, -63.4) * mm, "end": v(3.81, -43.4) * mm});
            skLineSegment(sketch, "E45.9", {"start": v(63.4, 23.8) * mm, "end": v(43.4, 3.81) * mm});
            skLineSegment(sketch, "E45.10", {"start": v(43.4, 3.81) * mm, "end": v(3.81, 43.4) * mm});
            skLineSegment(sketch, "E45.11", {"start": v(3.81, 43.4) * mm, "end": v(23.8, 63.4) * mm});
            skLineSegment(sketch, "E45.12", {"start": v(23.8, 63.4) * mm, "end": v(-23.8, 63.4) * mm});
            skLineSegment(sketch, "E45.13", {"start": v(-23.8, 63.4) * mm, "end": v(-3.81, 43.4) * mm});
            skLineSegment(sketch, "E45.14", {"start": v(-23.8, -63.4) * mm, "end": v(23.8, -63.4) * mm});
            skLineSegment(sketch, "E45.15", {"start": v(-3.81, 43.4) * mm, "end": v(-43.4, 3.81) * mm});
            skLineSegment(sketch, "E46.0", {"start": v(15.8, 55.4) * mm, "end": v(-15.8, 55.4) * mm});
            skLineSegment(sketch, "E47.0", {"start": v(-55.4, 15.8) * mm, "end": v(-55.4, -15.8) * mm});
            skLineSegment(sketch, "E48.0", {"start": v(-15.8, -55.4) * mm, "end": v(15.8, -55.4) * mm});
            skLineSegment(sketch, "E49.0", {"start": v(55.4, -15.8) * mm, "end": v(55.4, 15.8) * mm});
            skSolve(sketch);
        }
        {
            var Q0;
            {var subQ1=sQuery(id+"F11.wireOp",EDGE,"E20");Q0=makeQuery(id+"F27.boolean.opBoolean","SPLIT",FACE,{"disambiguationData":[TD([makeQuery(id+"F27.opExtrude","SWEPT_FACE",FACE,{"disambiguationData":[OSD([sQuery(id+"F26.wireOp",EDGE,"E44.top")])]})])],"derivedFrom":makeQuery(id+"F12.boolean.opBoolean","COPY",FACE,{"derivedFrom":makeQuery(id+"F12.opExtrude","SWEPT_FACE",FACE,{"disambiguationData":[OSD([subQ1])]})})});}
            var sketch = newSketch(context, id + "F29", { "sketchPlane" : qUnion([Q0])});
            skCircle(sketch, "E50", {"center": v(0, 30) * mm, "radius": 5 * mm});
            skPoint(sketch, "E50.centerSnap0", {"position": v(0, 10) * mm});
            skSolve(sketch);
        }
        {
            var Q0;
            Q0 = qSketchRegion(id + "F29", true);
            extrude(context, id + "F30", {"entities" : qUnion([Q0]), "operationType" : NewBodyOperationType.REMOVE, "endBound" : BoundingType.THROUGH_ALL, "oppositeDirection" : true, "depth" : 25 * mm});
        }
        {
            var Q0;
            {var subQ1=sQuery(id+"F11.wireOp",EDGE,"E25");Q0=makeQuery(id+"F27.boolean.opBoolean","SPLIT",FACE,{"disambiguationData":[TD([makeQuery(id+"F27.opExtrude","SWEPT_FACE",FACE,{"disambiguationData":[OSD([sQuery(id+"F26.wireOp",EDGE,"E44.top")])]})])],"derivedFrom":makeQuery(id+"F12.boolean.opBoolean","COPY",FACE,{"derivedFrom":makeQuery(id+"F12.opExtrude","SWEPT_FACE",FACE,{"disambiguationData":[OSD([subQ1])]})})});}
            var sketch = newSketch(context, id + "F31", { "sketchPlane" : qUnion([Q0])});
            skCircle(sketch, "E51", {"center": v(0, 30) * mm, "radius": 5 * mm});
            skPoint(sketch, "E51.centerSnap0", {"position": v(0, 10) * mm});
            skCircle(sketch, "E52", {"center": v(15, 30) * mm, "radius": 3.75 * mm});
            skCircle(sketch, "E53", {"center": v(-15, 30) * mm, "radius": 3.75 * mm});
            skSolve(sketch);
        }
        {
            var Q0;
            Q0=makeQuery(id+"F31.imprint","IMPRINT",FACE,{"disambiguationData":[TD([[makeQuery(id+"F31.imprint","IMPRINT",EDGE,{"derivedFrom":sQuery(id+"F31.wireOp",EDGE,"E51")}),1.0]])]});
            extrude(context, id + "F32", {"entities" : qUnion([Q0]), "operationType" : NewBodyOperationType.REMOVE, "endBound" : BoundingType.THROUGH_ALL, "oppositeDirection" : true, "depth" : 25 * mm});
        }
        {
            var Q0;
            Q0=makeQuery(id+"F1.opExtrude","CAP_FACE",FACE,{"disambiguationData":[OSD([sQuery(id+"F0.wireOp",EDGE,"E0.0"),sQuery(id+"F0.wireOp",EDGE,"E0.1"),sQuery(id+"F0.wireOp",EDGE,"E0.2"),sQuery(id+"F0.wireOp",EDGE,"E0.3"),sQuery(id+"F0.wireOp",EDGE,"E0.4"),sQuery(id+"F0.wireOp",EDGE,"E0.5"),sQuery(id+"F0.wireOp",EDGE,"E0.6"),sQuery(id+"F0.wireOp",EDGE,"E0.7")])],"isStart":false});
            var sketch = newSketch(context, id + "F33", { "sketchPlane" : qUnion([Q0])});
            skCircle(sketch, "E54", {"center": v(-8.46, -61.5) * mm, "radius": 2.5 * mm});
            skCircle(sketch, "E55", {"center": v(8.46, -61.5) * mm, "radius": 2.5 * mm});
            skCircle(sketch, "E56.MirrorC", {"center": v(-8.46, 61.5) * mm, "radius": 2.5 * mm});
            skCircle(sketch, "E57.MirrorC", {"center": v(8.46, 61.5) * mm, "radius": 2.5 * mm});
            skCircle(sketch, "E58", {"center": v(-61.5, 8.46) * mm, "radius": 2.5 * mm});
            skCircle(sketch, "E59", {"center": v(-61.5, -8.46) * mm, "radius": 2.5 * mm});
            skCircle(sketch, "E60.MirrorC", {"center": v(61.5, 8.46) * mm, "radius": 2.5 * mm});
            skCircle(sketch, "E61.MirrorC", {"center": v(61.5, -8.46) * mm, "radius": 2.5 * mm});
            skCircle(sketch, "E62", {"center": v(-61.5, 8.46) * mm, "radius": 4 * mm});
            skCircle(sketch, "E63", {"center": v(-61.5, -8.46) * mm, "radius": 4 * mm});
            skCircle(sketch, "E64", {"center": v(-8.46, -61.5) * mm, "radius": 4 * mm});
            skCircle(sketch, "E65", {"center": v(8.46, -61.5) * mm, "radius": 4 * mm});
            skCircle(sketch, "E66", {"center": v(61.5, -8.46) * mm, "radius": 4 * mm});
            skCircle(sketch, "E67", {"center": v(61.5, 8.46) * mm, "radius": 4 * mm});
            skCircle(sketch, "E68", {"center": v(8.46, 61.5) * mm, "radius": 4 * mm});
            skCircle(sketch, "E69", {"center": v(-8.46, 61.5) * mm, "radius": 4 * mm});
            skSolve(sketch);
        }
        {
            var Q0;
            {var subQ0=sQuery(id+"F33.wireOp",EDGE,"E56.MirrorC");var subQ1=sQuery(id+"F0.wireOp",EDGE,"E0.6");var subQ2=makeQuery(id+"F25.opFillet","BLEND_EDGE",EDGE,{"blendedFrom":[makeQuery(id+"F1.opExtrude","CAP_EDGE",EDGE,{"disambiguationData":[OSD([subQ1])],"isStart":false}),makeQuery(id+"F1.opExtrude","CAP_FACE",FACE,{"disambiguationData":[OSD([sQuery(id+"F0.wireOp",EDGE,"E0.0"),sQuery(id+"F0.wireOp",EDGE,"E0.1"),sQuery(id+"F0.wireOp",EDGE,"E0.2"),sQuery(id+"F0.wireOp",EDGE,"E0.3"),sQuery(id+"F0.wireOp",EDGE,"E0.4"),sQuery(id+"F0.wireOp",EDGE,"E0.5"),subQ1,sQuery(id+"F0.wireOp",EDGE,"E0.7")])],"isStart":false})],"blendedInto":[makeQuery(id+"F1.opExtrude","CAP_FACE",FACE,{"disambiguationData":[OSD([sQuery(id+"F0.wireOp",EDGE,"E0.0"),sQuery(id+"F0.wireOp",EDGE,"E0.1"),sQuery(id+"F0.wireOp",EDGE,"E0.2"),sQuery(id+"F0.wireOp",EDGE,"E0.3"),sQuery(id+"F0.wireOp",EDGE,"E0.4"),sQuery(id+"F0.wireOp",EDGE,"E0.5"),subQ1,sQuery(id+"F0.wireOp",EDGE,"E0.7")])],"isStart":false})]});var subQ3=makeQuery(id+"F33.imprint","INTERSECT",VERTEX,{"disambiguationData":[OD(0.0)],"derivedFrom":[subQ2,subQ0]});Q0=makeQuery(id+"F33.imprint","IMPRINT",FACE,{"disambiguationData":[TD([[makeQuery(id+"F33.imprint","IMPRINT",EDGE,{"disambiguationData":[TD([[subQ3,-1.0]])],"derivedFrom":subQ0}),-1.0]])]});}
            var Q1;
            {var subQ0=sQuery(id+"F33.wireOp",EDGE,"E56.MirrorC");var subQ1=sQuery(id+"F0.wireOp",EDGE,"E0.6");var subQ2=makeQuery(id+"F25.opFillet","BLEND_EDGE",EDGE,{"blendedFrom":[makeQuery(id+"F1.opExtrude","CAP_EDGE",EDGE,{"disambiguationData":[OSD([subQ1])],"isStart":false}),makeQuery(id+"F1.opExtrude","CAP_FACE",FACE,{"disambiguationData":[OSD([sQuery(id+"F0.wireOp",EDGE,"E0.0"),sQuery(id+"F0.wireOp",EDGE,"E0.1"),sQuery(id+"F0.wireOp",EDGE,"E0.2"),sQuery(id+"F0.wireOp",EDGE,"E0.3"),sQuery(id+"F0.wireOp",EDGE,"E0.4"),sQuery(id+"F0.wireOp",EDGE,"E0.5"),subQ1,sQuery(id+"F0.wireOp",EDGE,"E0.7")])],"isStart":false})],"blendedInto":[makeQuery(id+"F1.opExtrude","CAP_FACE",FACE,{"disambiguationData":[OSD([sQuery(id+"F0.wireOp",EDGE,"E0.0"),sQuery(id+"F0.wireOp",EDGE,"E0.1"),sQuery(id+"F0.wireOp",EDGE,"E0.2"),sQuery(id+"F0.wireOp",EDGE,"E0.3"),sQuery(id+"F0.wireOp",EDGE,"E0.4"),sQuery(id+"F0.wireOp",EDGE,"E0.5"),subQ1,sQuery(id+"F0.wireOp",EDGE,"E0.7")])],"isStart":false})]});var subQ3=makeQuery(id+"F33.imprint","INTERSECT",VERTEX,{"disambiguationData":[OD(0.0)],"derivedFrom":[subQ2,subQ0]});Q1=makeQuery(id+"F33.imprint","IMPRINT",FACE,{"disambiguationData":[TD([[makeQuery(id+"F33.imprint","IMPRINT",EDGE,{"disambiguationData":[TD([[subQ3,1.0]])],"derivedFrom":subQ0}),-1.0]])]});}
            var Q2;
            {var subQ0=sQuery(id+"F33.wireOp",EDGE,"E57.MirrorC");var subQ1=sQuery(id+"F0.wireOp",EDGE,"E0.6");var subQ2=makeQuery(id+"F25.opFillet","BLEND_EDGE",EDGE,{"blendedFrom":[makeQuery(id+"F1.opExtrude","CAP_EDGE",EDGE,{"disambiguationData":[OSD([subQ1])],"isStart":false}),makeQuery(id+"F1.opExtrude","CAP_FACE",FACE,{"disambiguationData":[OSD([sQuery(id+"F0.wireOp",EDGE,"E0.0"),sQuery(id+"F0.wireOp",EDGE,"E0.1"),sQuery(id+"F0.wireOp",EDGE,"E0.2"),sQuery(id+"F0.wireOp",EDGE,"E0.3"),sQuery(id+"F0.wireOp",EDGE,"E0.4"),sQuery(id+"F0.wireOp",EDGE,"E0.5"),subQ1,sQuery(id+"F0.wireOp",EDGE,"E0.7")])],"isStart":false})],"blendedInto":[makeQuery(id+"F1.opExtrude","CAP_FACE",FACE,{"disambiguationData":[OSD([sQuery(id+"F0.wireOp",EDGE,"E0.0"),sQuery(id+"F0.wireOp",EDGE,"E0.1"),sQuery(id+"F0.wireOp",EDGE,"E0.2"),sQuery(id+"F0.wireOp",EDGE,"E0.3"),sQuery(id+"F0.wireOp",EDGE,"E0.4"),sQuery(id+"F0.wireOp",EDGE,"E0.5"),subQ1,sQuery(id+"F0.wireOp",EDGE,"E0.7")])],"isStart":false})]});var subQ3=makeQuery(id+"F33.imprint","INTERSECT",VERTEX,{"disambiguationData":[OD(0.0)],"derivedFrom":[subQ2,subQ0]});Q2=makeQuery(id+"F33.imprint","IMPRINT",FACE,{"disambiguationData":[TD([[makeQuery(id+"F33.imprint","IMPRINT",EDGE,{"disambiguationData":[TD([[subQ3,1.0]])],"derivedFrom":subQ0}),-1.0]])]});}
            var Q3;
            {var subQ0=sQuery(id+"F33.wireOp",EDGE,"E57.MirrorC");var subQ1=sQuery(id+"F0.wireOp",EDGE,"E0.6");var subQ2=makeQuery(id+"F25.opFillet","BLEND_EDGE",EDGE,{"blendedFrom":[makeQuery(id+"F1.opExtrude","CAP_EDGE",EDGE,{"disambiguationData":[OSD([subQ1])],"isStart":false}),makeQuery(id+"F1.opExtrude","CAP_FACE",FACE,{"disambiguationData":[OSD([sQuery(id+"F0.wireOp",EDGE,"E0.0"),sQuery(id+"F0.wireOp",EDGE,"E0.1"),sQuery(id+"F0.wireOp",EDGE,"E0.2"),sQuery(id+"F0.wireOp",EDGE,"E0.3"),sQuery(id+"F0.wireOp",EDGE,"E0.4"),sQuery(id+"F0.wireOp",EDGE,"E0.5"),subQ1,sQuery(id+"F0.wireOp",EDGE,"E0.7")])],"isStart":false})],"blendedInto":[makeQuery(id+"F1.opExtrude","CAP_FACE",FACE,{"disambiguationData":[OSD([sQuery(id+"F0.wireOp",EDGE,"E0.0"),sQuery(id+"F0.wireOp",EDGE,"E0.1"),sQuery(id+"F0.wireOp",EDGE,"E0.2"),sQuery(id+"F0.wireOp",EDGE,"E0.3"),sQuery(id+"F0.wireOp",EDGE,"E0.4"),sQuery(id+"F0.wireOp",EDGE,"E0.5"),subQ1,sQuery(id+"F0.wireOp",EDGE,"E0.7")])],"isStart":false})]});var subQ3=makeQuery(id+"F33.imprint","INTERSECT",VERTEX,{"disambiguationData":[OD(0.0)],"derivedFrom":[subQ2,subQ0]});Q3=makeQuery(id+"F33.imprint","IMPRINT",FACE,{"disambiguationData":[TD([[makeQuery(id+"F33.imprint","IMPRINT",EDGE,{"disambiguationData":[TD([[subQ3,-1.0]])],"derivedFrom":subQ0}),-1.0]])]});}
            var Q4;
            {var subQ0=sQuery(id+"F33.wireOp",EDGE,"E58");var subQ1=sQuery(id+"F0.wireOp",EDGE,"E0.4");var subQ2=makeQuery(id+"F25.opFillet","BLEND_EDGE",EDGE,{"blendedFrom":[makeQuery(id+"F1.opExtrude","CAP_EDGE",EDGE,{"disambiguationData":[OSD([subQ1])],"isStart":false}),makeQuery(id+"F1.opExtrude","CAP_FACE",FACE,{"disambiguationData":[OSD([sQuery(id+"F0.wireOp",EDGE,"E0.0"),sQuery(id+"F0.wireOp",EDGE,"E0.1"),sQuery(id+"F0.wireOp",EDGE,"E0.2"),sQuery(id+"F0.wireOp",EDGE,"E0.3"),subQ1,sQuery(id+"F0.wireOp",EDGE,"E0.5"),sQuery(id+"F0.wireOp",EDGE,"E0.6"),sQuery(id+"F0.wireOp",EDGE,"E0.7")])],"isStart":false})],"blendedInto":[makeQuery(id+"F1.opExtrude","CAP_FACE",FACE,{"disambiguationData":[OSD([sQuery(id+"F0.wireOp",EDGE,"E0.0"),sQuery(id+"F0.wireOp",EDGE,"E0.1"),sQuery(id+"F0.wireOp",EDGE,"E0.2"),sQuery(id+"F0.wireOp",EDGE,"E0.3"),subQ1,sQuery(id+"F0.wireOp",EDGE,"E0.5"),sQuery(id+"F0.wireOp",EDGE,"E0.6"),sQuery(id+"F0.wireOp",EDGE,"E0.7")])],"isStart":false})]});var subQ3=makeQuery(id+"F33.imprint","INTERSECT",VERTEX,{"disambiguationData":[OD(0.0)],"derivedFrom":[subQ2,subQ0]});Q4=makeQuery(id+"F33.imprint","IMPRINT",FACE,{"disambiguationData":[TD([[makeQuery(id+"F33.imprint","IMPRINT",EDGE,{"disambiguationData":[TD([[subQ3,-1.0]])],"derivedFrom":subQ0}),1.0]])]});}
            var Q5;
            {var subQ0=sQuery(id+"F33.wireOp",EDGE,"E58");var subQ1=sQuery(id+"F0.wireOp",EDGE,"E0.4");var subQ2=makeQuery(id+"F25.opFillet","BLEND_EDGE",EDGE,{"blendedFrom":[makeQuery(id+"F1.opExtrude","CAP_EDGE",EDGE,{"disambiguationData":[OSD([subQ1])],"isStart":false}),makeQuery(id+"F1.opExtrude","CAP_FACE",FACE,{"disambiguationData":[OSD([sQuery(id+"F0.wireOp",EDGE,"E0.0"),sQuery(id+"F0.wireOp",EDGE,"E0.1"),sQuery(id+"F0.wireOp",EDGE,"E0.2"),sQuery(id+"F0.wireOp",EDGE,"E0.3"),subQ1,sQuery(id+"F0.wireOp",EDGE,"E0.5"),sQuery(id+"F0.wireOp",EDGE,"E0.6"),sQuery(id+"F0.wireOp",EDGE,"E0.7")])],"isStart":false})],"blendedInto":[makeQuery(id+"F1.opExtrude","CAP_FACE",FACE,{"disambiguationData":[OSD([sQuery(id+"F0.wireOp",EDGE,"E0.0"),sQuery(id+"F0.wireOp",EDGE,"E0.1"),sQuery(id+"F0.wireOp",EDGE,"E0.2"),sQuery(id+"F0.wireOp",EDGE,"E0.3"),subQ1,sQuery(id+"F0.wireOp",EDGE,"E0.5"),sQuery(id+"F0.wireOp",EDGE,"E0.6"),sQuery(id+"F0.wireOp",EDGE,"E0.7")])],"isStart":false})]});var subQ3=makeQuery(id+"F33.imprint","INTERSECT",VERTEX,{"disambiguationData":[OD(0.0)],"derivedFrom":[subQ2,subQ0]});Q5=makeQuery(id+"F33.imprint","IMPRINT",FACE,{"disambiguationData":[TD([[makeQuery(id+"F33.imprint","IMPRINT",EDGE,{"disambiguationData":[TD([[subQ3,1.0]])],"derivedFrom":subQ0}),1.0]])]});}
            var Q6;
            {var subQ0=sQuery(id+"F33.wireOp",EDGE,"E59");var subQ1=sQuery(id+"F0.wireOp",EDGE,"E0.4");var subQ2=makeQuery(id+"F25.opFillet","BLEND_EDGE",EDGE,{"blendedFrom":[makeQuery(id+"F1.opExtrude","CAP_EDGE",EDGE,{"disambiguationData":[OSD([subQ1])],"isStart":false}),makeQuery(id+"F1.opExtrude","CAP_FACE",FACE,{"disambiguationData":[OSD([sQuery(id+"F0.wireOp",EDGE,"E0.0"),sQuery(id+"F0.wireOp",EDGE,"E0.1"),sQuery(id+"F0.wireOp",EDGE,"E0.2"),sQuery(id+"F0.wireOp",EDGE,"E0.3"),subQ1,sQuery(id+"F0.wireOp",EDGE,"E0.5"),sQuery(id+"F0.wireOp",EDGE,"E0.6"),sQuery(id+"F0.wireOp",EDGE,"E0.7")])],"isStart":false})],"blendedInto":[makeQuery(id+"F1.opExtrude","CAP_FACE",FACE,{"disambiguationData":[OSD([sQuery(id+"F0.wireOp",EDGE,"E0.0"),sQuery(id+"F0.wireOp",EDGE,"E0.1"),sQuery(id+"F0.wireOp",EDGE,"E0.2"),sQuery(id+"F0.wireOp",EDGE,"E0.3"),subQ1,sQuery(id+"F0.wireOp",EDGE,"E0.5"),sQuery(id+"F0.wireOp",EDGE,"E0.6"),sQuery(id+"F0.wireOp",EDGE,"E0.7")])],"isStart":false})]});var subQ3=makeQuery(id+"F33.imprint","INTERSECT",VERTEX,{"disambiguationData":[OD(0.0)],"derivedFrom":[subQ2,subQ0]});Q6=makeQuery(id+"F33.imprint","IMPRINT",FACE,{"disambiguationData":[TD([[makeQuery(id+"F33.imprint","IMPRINT",EDGE,{"disambiguationData":[TD([[subQ3,1.0]])],"derivedFrom":subQ0}),1.0]])]});}
            var Q7;
            {var subQ0=sQuery(id+"F33.wireOp",EDGE,"E59");var subQ1=sQuery(id+"F0.wireOp",EDGE,"E0.4");var subQ2=makeQuery(id+"F25.opFillet","BLEND_EDGE",EDGE,{"blendedFrom":[makeQuery(id+"F1.opExtrude","CAP_EDGE",EDGE,{"disambiguationData":[OSD([subQ1])],"isStart":false}),makeQuery(id+"F1.opExtrude","CAP_FACE",FACE,{"disambiguationData":[OSD([sQuery(id+"F0.wireOp",EDGE,"E0.0"),sQuery(id+"F0.wireOp",EDGE,"E0.1"),sQuery(id+"F0.wireOp",EDGE,"E0.2"),sQuery(id+"F0.wireOp",EDGE,"E0.3"),subQ1,sQuery(id+"F0.wireOp",EDGE,"E0.5"),sQuery(id+"F0.wireOp",EDGE,"E0.6"),sQuery(id+"F0.wireOp",EDGE,"E0.7")])],"isStart":false})],"blendedInto":[makeQuery(id+"F1.opExtrude","CAP_FACE",FACE,{"disambiguationData":[OSD([sQuery(id+"F0.wireOp",EDGE,"E0.0"),sQuery(id+"F0.wireOp",EDGE,"E0.1"),sQuery(id+"F0.wireOp",EDGE,"E0.2"),sQuery(id+"F0.wireOp",EDGE,"E0.3"),subQ1,sQuery(id+"F0.wireOp",EDGE,"E0.5"),sQuery(id+"F0.wireOp",EDGE,"E0.6"),sQuery(id+"F0.wireOp",EDGE,"E0.7")])],"isStart":false})]});var subQ3=makeQuery(id+"F33.imprint","INTERSECT",VERTEX,{"disambiguationData":[OD(0.0)],"derivedFrom":[subQ2,subQ0]});Q7=makeQuery(id+"F33.imprint","IMPRINT",FACE,{"disambiguationData":[TD([[makeQuery(id+"F33.imprint","IMPRINT",EDGE,{"disambiguationData":[TD([[subQ3,-1.0]])],"derivedFrom":subQ0}),1.0]])]});}
            var Q8;
            {var subQ0=sQuery(id+"F33.wireOp",EDGE,"E61.MirrorC");var subQ1=sQuery(id+"F0.wireOp",EDGE,"E0.0");var subQ2=makeQuery(id+"F25.opFillet","BLEND_EDGE",EDGE,{"blendedFrom":[makeQuery(id+"F1.opExtrude","CAP_EDGE",EDGE,{"disambiguationData":[OSD([subQ1])],"isStart":false}),makeQuery(id+"F1.opExtrude","CAP_FACE",FACE,{"disambiguationData":[OSD([subQ1,sQuery(id+"F0.wireOp",EDGE,"E0.1"),sQuery(id+"F0.wireOp",EDGE,"E0.2"),sQuery(id+"F0.wireOp",EDGE,"E0.3"),sQuery(id+"F0.wireOp",EDGE,"E0.4"),sQuery(id+"F0.wireOp",EDGE,"E0.5"),sQuery(id+"F0.wireOp",EDGE,"E0.6"),sQuery(id+"F0.wireOp",EDGE,"E0.7")])],"isStart":false})],"blendedInto":[makeQuery(id+"F1.opExtrude","CAP_FACE",FACE,{"disambiguationData":[OSD([subQ1,sQuery(id+"F0.wireOp",EDGE,"E0.1"),sQuery(id+"F0.wireOp",EDGE,"E0.2"),sQuery(id+"F0.wireOp",EDGE,"E0.3"),sQuery(id+"F0.wireOp",EDGE,"E0.4"),sQuery(id+"F0.wireOp",EDGE,"E0.5"),sQuery(id+"F0.wireOp",EDGE,"E0.6"),sQuery(id+"F0.wireOp",EDGE,"E0.7")])],"isStart":false})]});var subQ3=makeQuery(id+"F33.imprint","INTERSECT",VERTEX,{"disambiguationData":[OD(0.0)],"derivedFrom":[subQ2,subQ0]});Q8=makeQuery(id+"F33.imprint","IMPRINT",FACE,{"disambiguationData":[TD([[makeQuery(id+"F33.imprint","IMPRINT",EDGE,{"disambiguationData":[TD([[subQ3,-1.0]])],"derivedFrom":subQ0}),-1.0]])]});}
            var Q9;
            {var subQ0=sQuery(id+"F33.wireOp",EDGE,"E61.MirrorC");var subQ1=sQuery(id+"F0.wireOp",EDGE,"E0.0");var subQ2=makeQuery(id+"F25.opFillet","BLEND_EDGE",EDGE,{"blendedFrom":[makeQuery(id+"F1.opExtrude","CAP_EDGE",EDGE,{"disambiguationData":[OSD([subQ1])],"isStart":false}),makeQuery(id+"F1.opExtrude","CAP_FACE",FACE,{"disambiguationData":[OSD([subQ1,sQuery(id+"F0.wireOp",EDGE,"E0.1"),sQuery(id+"F0.wireOp",EDGE,"E0.2"),sQuery(id+"F0.wireOp",EDGE,"E0.3"),sQuery(id+"F0.wireOp",EDGE,"E0.4"),sQuery(id+"F0.wireOp",EDGE,"E0.5"),sQuery(id+"F0.wireOp",EDGE,"E0.6"),sQuery(id+"F0.wireOp",EDGE,"E0.7")])],"isStart":false})],"blendedInto":[makeQuery(id+"F1.opExtrude","CAP_FACE",FACE,{"disambiguationData":[OSD([subQ1,sQuery(id+"F0.wireOp",EDGE,"E0.1"),sQuery(id+"F0.wireOp",EDGE,"E0.2"),sQuery(id+"F0.wireOp",EDGE,"E0.3"),sQuery(id+"F0.wireOp",EDGE,"E0.4"),sQuery(id+"F0.wireOp",EDGE,"E0.5"),sQuery(id+"F0.wireOp",EDGE,"E0.6"),sQuery(id+"F0.wireOp",EDGE,"E0.7")])],"isStart":false})]});var subQ3=makeQuery(id+"F33.imprint","INTERSECT",VERTEX,{"disambiguationData":[OD(0.0)],"derivedFrom":[subQ2,subQ0]});Q9=makeQuery(id+"F33.imprint","IMPRINT",FACE,{"disambiguationData":[TD([[makeQuery(id+"F33.imprint","IMPRINT",EDGE,{"disambiguationData":[TD([[subQ3,1.0]])],"derivedFrom":subQ0}),-1.0]])]});}
            var Q10;
            {var subQ0=sQuery(id+"F33.wireOp",EDGE,"E60.MirrorC");var subQ1=sQuery(id+"F0.wireOp",EDGE,"E0.0");var subQ2=makeQuery(id+"F25.opFillet","BLEND_EDGE",EDGE,{"blendedFrom":[makeQuery(id+"F1.opExtrude","CAP_EDGE",EDGE,{"disambiguationData":[OSD([subQ1])],"isStart":false}),makeQuery(id+"F1.opExtrude","CAP_FACE",FACE,{"disambiguationData":[OSD([subQ1,sQuery(id+"F0.wireOp",EDGE,"E0.1"),sQuery(id+"F0.wireOp",EDGE,"E0.2"),sQuery(id+"F0.wireOp",EDGE,"E0.3"),sQuery(id+"F0.wireOp",EDGE,"E0.4"),sQuery(id+"F0.wireOp",EDGE,"E0.5"),sQuery(id+"F0.wireOp",EDGE,"E0.6"),sQuery(id+"F0.wireOp",EDGE,"E0.7")])],"isStart":false})],"blendedInto":[makeQuery(id+"F1.opExtrude","CAP_FACE",FACE,{"disambiguationData":[OSD([subQ1,sQuery(id+"F0.wireOp",EDGE,"E0.1"),sQuery(id+"F0.wireOp",EDGE,"E0.2"),sQuery(id+"F0.wireOp",EDGE,"E0.3"),sQuery(id+"F0.wireOp",EDGE,"E0.4"),sQuery(id+"F0.wireOp",EDGE,"E0.5"),sQuery(id+"F0.wireOp",EDGE,"E0.6"),sQuery(id+"F0.wireOp",EDGE,"E0.7")])],"isStart":false})]});var subQ3=makeQuery(id+"F33.imprint","INTERSECT",VERTEX,{"disambiguationData":[OD(0.0)],"derivedFrom":[subQ2,subQ0]});Q10=makeQuery(id+"F33.imprint","IMPRINT",FACE,{"disambiguationData":[TD([[makeQuery(id+"F33.imprint","IMPRINT",EDGE,{"disambiguationData":[TD([[subQ3,-1.0]])],"derivedFrom":subQ0}),-1.0]])]});}
            var Q11;
            {var subQ0=sQuery(id+"F33.wireOp",EDGE,"E60.MirrorC");var subQ1=sQuery(id+"F0.wireOp",EDGE,"E0.0");var subQ2=makeQuery(id+"F25.opFillet","BLEND_EDGE",EDGE,{"blendedFrom":[makeQuery(id+"F1.opExtrude","CAP_EDGE",EDGE,{"disambiguationData":[OSD([subQ1])],"isStart":false}),makeQuery(id+"F1.opExtrude","CAP_FACE",FACE,{"disambiguationData":[OSD([subQ1,sQuery(id+"F0.wireOp",EDGE,"E0.1"),sQuery(id+"F0.wireOp",EDGE,"E0.2"),sQuery(id+"F0.wireOp",EDGE,"E0.3"),sQuery(id+"F0.wireOp",EDGE,"E0.4"),sQuery(id+"F0.wireOp",EDGE,"E0.5"),sQuery(id+"F0.wireOp",EDGE,"E0.6"),sQuery(id+"F0.wireOp",EDGE,"E0.7")])],"isStart":false})],"blendedInto":[makeQuery(id+"F1.opExtrude","CAP_FACE",FACE,{"disambiguationData":[OSD([subQ1,sQuery(id+"F0.wireOp",EDGE,"E0.1"),sQuery(id+"F0.wireOp",EDGE,"E0.2"),sQuery(id+"F0.wireOp",EDGE,"E0.3"),sQuery(id+"F0.wireOp",EDGE,"E0.4"),sQuery(id+"F0.wireOp",EDGE,"E0.5"),sQuery(id+"F0.wireOp",EDGE,"E0.6"),sQuery(id+"F0.wireOp",EDGE,"E0.7")])],"isStart":false})]});var subQ3=makeQuery(id+"F33.imprint","INTERSECT",VERTEX,{"disambiguationData":[OD(0.0)],"derivedFrom":[subQ2,subQ0]});Q11=makeQuery(id+"F33.imprint","IMPRINT",FACE,{"disambiguationData":[TD([[makeQuery(id+"F33.imprint","IMPRINT",EDGE,{"disambiguationData":[TD([[subQ3,1.0]])],"derivedFrom":subQ0}),-1.0]])]});}
            var Q12;
            {var subQ0=sQuery(id+"F33.wireOp",EDGE,"E54");var subQ1=sQuery(id+"F0.wireOp",EDGE,"E0.2");var subQ2=makeQuery(id+"F25.opFillet","BLEND_EDGE",EDGE,{"blendedFrom":[makeQuery(id+"F1.opExtrude","CAP_EDGE",EDGE,{"disambiguationData":[OSD([subQ1])],"isStart":false}),makeQuery(id+"F1.opExtrude","CAP_FACE",FACE,{"disambiguationData":[OSD([sQuery(id+"F0.wireOp",EDGE,"E0.0"),sQuery(id+"F0.wireOp",EDGE,"E0.1"),subQ1,sQuery(id+"F0.wireOp",EDGE,"E0.3"),sQuery(id+"F0.wireOp",EDGE,"E0.4"),sQuery(id+"F0.wireOp",EDGE,"E0.5"),sQuery(id+"F0.wireOp",EDGE,"E0.6"),sQuery(id+"F0.wireOp",EDGE,"E0.7")])],"isStart":false})],"blendedInto":[makeQuery(id+"F1.opExtrude","CAP_FACE",FACE,{"disambiguationData":[OSD([sQuery(id+"F0.wireOp",EDGE,"E0.0"),sQuery(id+"F0.wireOp",EDGE,"E0.1"),subQ1,sQuery(id+"F0.wireOp",EDGE,"E0.3"),sQuery(id+"F0.wireOp",EDGE,"E0.4"),sQuery(id+"F0.wireOp",EDGE,"E0.5"),sQuery(id+"F0.wireOp",EDGE,"E0.6"),sQuery(id+"F0.wireOp",EDGE,"E0.7")])],"isStart":false})]});var subQ3=makeQuery(id+"F33.imprint","INTERSECT",VERTEX,{"disambiguationData":[OD(0.0)],"derivedFrom":[subQ2,subQ0]});Q12=makeQuery(id+"F33.imprint","IMPRINT",FACE,{"disambiguationData":[TD([[makeQuery(id+"F33.imprint","IMPRINT",EDGE,{"disambiguationData":[TD([[subQ3,-1.0]])],"derivedFrom":subQ0}),1.0]])]});}
            var Q13;
            {var subQ0=sQuery(id+"F33.wireOp",EDGE,"E54");var subQ1=sQuery(id+"F0.wireOp",EDGE,"E0.2");var subQ2=makeQuery(id+"F25.opFillet","BLEND_EDGE",EDGE,{"blendedFrom":[makeQuery(id+"F1.opExtrude","CAP_EDGE",EDGE,{"disambiguationData":[OSD([subQ1])],"isStart":false}),makeQuery(id+"F1.opExtrude","CAP_FACE",FACE,{"disambiguationData":[OSD([sQuery(id+"F0.wireOp",EDGE,"E0.0"),sQuery(id+"F0.wireOp",EDGE,"E0.1"),subQ1,sQuery(id+"F0.wireOp",EDGE,"E0.3"),sQuery(id+"F0.wireOp",EDGE,"E0.4"),sQuery(id+"F0.wireOp",EDGE,"E0.5"),sQuery(id+"F0.wireOp",EDGE,"E0.6"),sQuery(id+"F0.wireOp",EDGE,"E0.7")])],"isStart":false})],"blendedInto":[makeQuery(id+"F1.opExtrude","CAP_FACE",FACE,{"disambiguationData":[OSD([sQuery(id+"F0.wireOp",EDGE,"E0.0"),sQuery(id+"F0.wireOp",EDGE,"E0.1"),subQ1,sQuery(id+"F0.wireOp",EDGE,"E0.3"),sQuery(id+"F0.wireOp",EDGE,"E0.4"),sQuery(id+"F0.wireOp",EDGE,"E0.5"),sQuery(id+"F0.wireOp",EDGE,"E0.6"),sQuery(id+"F0.wireOp",EDGE,"E0.7")])],"isStart":false})]});var subQ3=makeQuery(id+"F33.imprint","INTERSECT",VERTEX,{"disambiguationData":[OD(0.0)],"derivedFrom":[subQ2,subQ0]});Q13=makeQuery(id+"F33.imprint","IMPRINT",FACE,{"disambiguationData":[TD([[makeQuery(id+"F33.imprint","IMPRINT",EDGE,{"disambiguationData":[TD([[subQ3,1.0]])],"derivedFrom":subQ0}),1.0]])]});}
            var Q14;
            {var subQ0=sQuery(id+"F33.wireOp",EDGE,"E55");var subQ1=sQuery(id+"F0.wireOp",EDGE,"E0.2");var subQ2=makeQuery(id+"F25.opFillet","BLEND_EDGE",EDGE,{"blendedFrom":[makeQuery(id+"F1.opExtrude","CAP_EDGE",EDGE,{"disambiguationData":[OSD([subQ1])],"isStart":false}),makeQuery(id+"F1.opExtrude","CAP_FACE",FACE,{"disambiguationData":[OSD([sQuery(id+"F0.wireOp",EDGE,"E0.0"),sQuery(id+"F0.wireOp",EDGE,"E0.1"),subQ1,sQuery(id+"F0.wireOp",EDGE,"E0.3"),sQuery(id+"F0.wireOp",EDGE,"E0.4"),sQuery(id+"F0.wireOp",EDGE,"E0.5"),sQuery(id+"F0.wireOp",EDGE,"E0.6"),sQuery(id+"F0.wireOp",EDGE,"E0.7")])],"isStart":false})],"blendedInto":[makeQuery(id+"F1.opExtrude","CAP_FACE",FACE,{"disambiguationData":[OSD([sQuery(id+"F0.wireOp",EDGE,"E0.0"),sQuery(id+"F0.wireOp",EDGE,"E0.1"),subQ1,sQuery(id+"F0.wireOp",EDGE,"E0.3"),sQuery(id+"F0.wireOp",EDGE,"E0.4"),sQuery(id+"F0.wireOp",EDGE,"E0.5"),sQuery(id+"F0.wireOp",EDGE,"E0.6"),sQuery(id+"F0.wireOp",EDGE,"E0.7")])],"isStart":false})]});var subQ3=makeQuery(id+"F33.imprint","INTERSECT",VERTEX,{"disambiguationData":[OD(0.0)],"derivedFrom":[subQ2,subQ0]});Q14=makeQuery(id+"F33.imprint","IMPRINT",FACE,{"disambiguationData":[TD([[makeQuery(id+"F33.imprint","IMPRINT",EDGE,{"disambiguationData":[TD([[subQ3,-1.0]])],"derivedFrom":subQ0}),1.0]])]});}
            var Q15;
            {var subQ0=sQuery(id+"F33.wireOp",EDGE,"E55");var subQ1=sQuery(id+"F0.wireOp",EDGE,"E0.2");var subQ2=makeQuery(id+"F25.opFillet","BLEND_EDGE",EDGE,{"blendedFrom":[makeQuery(id+"F1.opExtrude","CAP_EDGE",EDGE,{"disambiguationData":[OSD([subQ1])],"isStart":false}),makeQuery(id+"F1.opExtrude","CAP_FACE",FACE,{"disambiguationData":[OSD([sQuery(id+"F0.wireOp",EDGE,"E0.0"),sQuery(id+"F0.wireOp",EDGE,"E0.1"),subQ1,sQuery(id+"F0.wireOp",EDGE,"E0.3"),sQuery(id+"F0.wireOp",EDGE,"E0.4"),sQuery(id+"F0.wireOp",EDGE,"E0.5"),sQuery(id+"F0.wireOp",EDGE,"E0.6"),sQuery(id+"F0.wireOp",EDGE,"E0.7")])],"isStart":false})],"blendedInto":[makeQuery(id+"F1.opExtrude","CAP_FACE",FACE,{"disambiguationData":[OSD([sQuery(id+"F0.wireOp",EDGE,"E0.0"),sQuery(id+"F0.wireOp",EDGE,"E0.1"),subQ1,sQuery(id+"F0.wireOp",EDGE,"E0.3"),sQuery(id+"F0.wireOp",EDGE,"E0.4"),sQuery(id+"F0.wireOp",EDGE,"E0.5"),sQuery(id+"F0.wireOp",EDGE,"E0.6"),sQuery(id+"F0.wireOp",EDGE,"E0.7")])],"isStart":false})]});var subQ3=makeQuery(id+"F33.imprint","INTERSECT",VERTEX,{"disambiguationData":[OD(0.0)],"derivedFrom":[subQ2,subQ0]});Q15=makeQuery(id+"F33.imprint","IMPRINT",FACE,{"disambiguationData":[TD([[makeQuery(id+"F33.imprint","IMPRINT",EDGE,{"disambiguationData":[TD([[subQ3,1.0]])],"derivedFrom":subQ0}),1.0]])]});}
            extrude(context, id + "F34", {"entities" : qUnion([Q0, Q1, Q2, Q3, Q4, Q5, Q6, Q7, Q8, Q9, Q10, Q11, Q12, Q13, Q14, Q15]), "operationType" : NewBodyOperationType.REMOVE, "oppositeDirection" : true, "depth" : 20 * mm});
        }
        {
            var Q0;
            {var subQ0=sQuery(id+"F33.wireOp",EDGE,"E58");var subQ1=sQuery(id+"F0.wireOp",EDGE,"E0.4");var subQ2=makeQuery(id+"F25.opFillet","BLEND_EDGE",EDGE,{"blendedFrom":[makeQuery(id+"F1.opExtrude","CAP_EDGE",EDGE,{"disambiguationData":[OSD([subQ1])],"isStart":false}),makeQuery(id+"F1.opExtrude","CAP_FACE",FACE,{"disambiguationData":[OSD([sQuery(id+"F0.wireOp",EDGE,"E0.0"),sQuery(id+"F0.wireOp",EDGE,"E0.1"),sQuery(id+"F0.wireOp",EDGE,"E0.2"),sQuery(id+"F0.wireOp",EDGE,"E0.3"),subQ1,sQuery(id+"F0.wireOp",EDGE,"E0.5"),sQuery(id+"F0.wireOp",EDGE,"E0.6"),sQuery(id+"F0.wireOp",EDGE,"E0.7")])],"isStart":false})],"blendedInto":[makeQuery(id+"F1.opExtrude","CAP_FACE",FACE,{"disambiguationData":[OSD([sQuery(id+"F0.wireOp",EDGE,"E0.0"),sQuery(id+"F0.wireOp",EDGE,"E0.1"),sQuery(id+"F0.wireOp",EDGE,"E0.2"),sQuery(id+"F0.wireOp",EDGE,"E0.3"),subQ1,sQuery(id+"F0.wireOp",EDGE,"E0.5"),sQuery(id+"F0.wireOp",EDGE,"E0.6"),sQuery(id+"F0.wireOp",EDGE,"E0.7")])],"isStart":false})]});var subQ3=makeQuery(id+"F33.imprint","INTERSECT",VERTEX,{"disambiguationData":[OD(0.0)],"derivedFrom":[subQ2,subQ0]});Q0=makeQuery(id+"F33.imprint","IMPRINT",FACE,{"disambiguationData":[TD([[makeQuery(id+"F33.imprint","IMPRINT",EDGE,{"disambiguationData":[TD([[subQ3,-1.0]])],"derivedFrom":subQ0}),-1.0]])]});}
            var Q1;
            {var subQ0=sQuery(id+"F33.wireOp",EDGE,"E58");var subQ1=sQuery(id+"F0.wireOp",EDGE,"E0.4");var subQ2=makeQuery(id+"F25.opFillet","BLEND_EDGE",EDGE,{"blendedFrom":[makeQuery(id+"F1.opExtrude","CAP_EDGE",EDGE,{"disambiguationData":[OSD([subQ1])],"isStart":false}),makeQuery(id+"F1.opExtrude","CAP_FACE",FACE,{"disambiguationData":[OSD([sQuery(id+"F0.wireOp",EDGE,"E0.0"),sQuery(id+"F0.wireOp",EDGE,"E0.1"),sQuery(id+"F0.wireOp",EDGE,"E0.2"),sQuery(id+"F0.wireOp",EDGE,"E0.3"),subQ1,sQuery(id+"F0.wireOp",EDGE,"E0.5"),sQuery(id+"F0.wireOp",EDGE,"E0.6"),sQuery(id+"F0.wireOp",EDGE,"E0.7")])],"isStart":false})],"blendedInto":[makeQuery(id+"F1.opExtrude","CAP_FACE",FACE,{"disambiguationData":[OSD([sQuery(id+"F0.wireOp",EDGE,"E0.0"),sQuery(id+"F0.wireOp",EDGE,"E0.1"),sQuery(id+"F0.wireOp",EDGE,"E0.2"),sQuery(id+"F0.wireOp",EDGE,"E0.3"),subQ1,sQuery(id+"F0.wireOp",EDGE,"E0.5"),sQuery(id+"F0.wireOp",EDGE,"E0.6"),sQuery(id+"F0.wireOp",EDGE,"E0.7")])],"isStart":false})]});var subQ3=makeQuery(id+"F33.imprint","INTERSECT",VERTEX,{"disambiguationData":[OD(0.0)],"derivedFrom":[subQ2,subQ0]});Q1=makeQuery(id+"F33.imprint","IMPRINT",FACE,{"disambiguationData":[TD([[makeQuery(id+"F33.imprint","IMPRINT",EDGE,{"disambiguationData":[TD([[subQ3,1.0]])],"derivedFrom":subQ0}),-1.0]])]});}
            var Q2;
            {var subQ0=sQuery(id+"F33.wireOp",EDGE,"E59");var subQ1=sQuery(id+"F0.wireOp",EDGE,"E0.4");var subQ2=makeQuery(id+"F25.opFillet","BLEND_EDGE",EDGE,{"blendedFrom":[makeQuery(id+"F1.opExtrude","CAP_EDGE",EDGE,{"disambiguationData":[OSD([subQ1])],"isStart":false}),makeQuery(id+"F1.opExtrude","CAP_FACE",FACE,{"disambiguationData":[OSD([sQuery(id+"F0.wireOp",EDGE,"E0.0"),sQuery(id+"F0.wireOp",EDGE,"E0.1"),sQuery(id+"F0.wireOp",EDGE,"E0.2"),sQuery(id+"F0.wireOp",EDGE,"E0.3"),subQ1,sQuery(id+"F0.wireOp",EDGE,"E0.5"),sQuery(id+"F0.wireOp",EDGE,"E0.6"),sQuery(id+"F0.wireOp",EDGE,"E0.7")])],"isStart":false})],"blendedInto":[makeQuery(id+"F1.opExtrude","CAP_FACE",FACE,{"disambiguationData":[OSD([sQuery(id+"F0.wireOp",EDGE,"E0.0"),sQuery(id+"F0.wireOp",EDGE,"E0.1"),sQuery(id+"F0.wireOp",EDGE,"E0.2"),sQuery(id+"F0.wireOp",EDGE,"E0.3"),subQ1,sQuery(id+"F0.wireOp",EDGE,"E0.5"),sQuery(id+"F0.wireOp",EDGE,"E0.6"),sQuery(id+"F0.wireOp",EDGE,"E0.7")])],"isStart":false})]});var subQ3=makeQuery(id+"F33.imprint","INTERSECT",VERTEX,{"disambiguationData":[OD(0.0)],"derivedFrom":[subQ2,subQ0]});Q2=makeQuery(id+"F33.imprint","IMPRINT",FACE,{"disambiguationData":[TD([[makeQuery(id+"F33.imprint","IMPRINT",EDGE,{"disambiguationData":[TD([[subQ3,1.0]])],"derivedFrom":subQ0}),-1.0]])]});}
            var Q3;
            {var subQ0=sQuery(id+"F33.wireOp",EDGE,"E59");var subQ1=sQuery(id+"F0.wireOp",EDGE,"E0.4");var subQ2=makeQuery(id+"F25.opFillet","BLEND_EDGE",EDGE,{"blendedFrom":[makeQuery(id+"F1.opExtrude","CAP_EDGE",EDGE,{"disambiguationData":[OSD([subQ1])],"isStart":false}),makeQuery(id+"F1.opExtrude","CAP_FACE",FACE,{"disambiguationData":[OSD([sQuery(id+"F0.wireOp",EDGE,"E0.0"),sQuery(id+"F0.wireOp",EDGE,"E0.1"),sQuery(id+"F0.wireOp",EDGE,"E0.2"),sQuery(id+"F0.wireOp",EDGE,"E0.3"),subQ1,sQuery(id+"F0.wireOp",EDGE,"E0.5"),sQuery(id+"F0.wireOp",EDGE,"E0.6"),sQuery(id+"F0.wireOp",EDGE,"E0.7")])],"isStart":false})],"blendedInto":[makeQuery(id+"F1.opExtrude","CAP_FACE",FACE,{"disambiguationData":[OSD([sQuery(id+"F0.wireOp",EDGE,"E0.0"),sQuery(id+"F0.wireOp",EDGE,"E0.1"),sQuery(id+"F0.wireOp",EDGE,"E0.2"),sQuery(id+"F0.wireOp",EDGE,"E0.3"),subQ1,sQuery(id+"F0.wireOp",EDGE,"E0.5"),sQuery(id+"F0.wireOp",EDGE,"E0.6"),sQuery(id+"F0.wireOp",EDGE,"E0.7")])],"isStart":false})]});var subQ3=makeQuery(id+"F33.imprint","INTERSECT",VERTEX,{"disambiguationData":[OD(0.0)],"derivedFrom":[subQ2,subQ0]});Q3=makeQuery(id+"F33.imprint","IMPRINT",FACE,{"disambiguationData":[TD([[makeQuery(id+"F33.imprint","IMPRINT",EDGE,{"disambiguationData":[TD([[subQ3,-1.0]])],"derivedFrom":subQ0}),-1.0]])]});}
            var Q4;
            {var subQ0=sQuery(id+"F33.wireOp",EDGE,"E56.MirrorC");var subQ1=sQuery(id+"F0.wireOp",EDGE,"E0.6");var subQ2=makeQuery(id+"F25.opFillet","BLEND_EDGE",EDGE,{"blendedFrom":[makeQuery(id+"F1.opExtrude","CAP_EDGE",EDGE,{"disambiguationData":[OSD([subQ1])],"isStart":false}),makeQuery(id+"F1.opExtrude","CAP_FACE",FACE,{"disambiguationData":[OSD([sQuery(id+"F0.wireOp",EDGE,"E0.0"),sQuery(id+"F0.wireOp",EDGE,"E0.1"),sQuery(id+"F0.wireOp",EDGE,"E0.2"),sQuery(id+"F0.wireOp",EDGE,"E0.3"),sQuery(id+"F0.wireOp",EDGE,"E0.4"),sQuery(id+"F0.wireOp",EDGE,"E0.5"),subQ1,sQuery(id+"F0.wireOp",EDGE,"E0.7")])],"isStart":false})],"blendedInto":[makeQuery(id+"F1.opExtrude","CAP_FACE",FACE,{"disambiguationData":[OSD([sQuery(id+"F0.wireOp",EDGE,"E0.0"),sQuery(id+"F0.wireOp",EDGE,"E0.1"),sQuery(id+"F0.wireOp",EDGE,"E0.2"),sQuery(id+"F0.wireOp",EDGE,"E0.3"),sQuery(id+"F0.wireOp",EDGE,"E0.4"),sQuery(id+"F0.wireOp",EDGE,"E0.5"),subQ1,sQuery(id+"F0.wireOp",EDGE,"E0.7")])],"isStart":false})]});var subQ3=makeQuery(id+"F33.imprint","INTERSECT",VERTEX,{"disambiguationData":[OD(0.0)],"derivedFrom":[subQ2,subQ0]});Q4=makeQuery(id+"F33.imprint","IMPRINT",FACE,{"disambiguationData":[TD([[makeQuery(id+"F33.imprint","IMPRINT",EDGE,{"disambiguationData":[TD([[subQ3,-1.0]])],"derivedFrom":subQ0}),1.0]])]});}
            var Q5;
            {var subQ0=sQuery(id+"F33.wireOp",EDGE,"E56.MirrorC");var subQ1=sQuery(id+"F0.wireOp",EDGE,"E0.6");var subQ2=makeQuery(id+"F25.opFillet","BLEND_EDGE",EDGE,{"blendedFrom":[makeQuery(id+"F1.opExtrude","CAP_EDGE",EDGE,{"disambiguationData":[OSD([subQ1])],"isStart":false}),makeQuery(id+"F1.opExtrude","CAP_FACE",FACE,{"disambiguationData":[OSD([sQuery(id+"F0.wireOp",EDGE,"E0.0"),sQuery(id+"F0.wireOp",EDGE,"E0.1"),sQuery(id+"F0.wireOp",EDGE,"E0.2"),sQuery(id+"F0.wireOp",EDGE,"E0.3"),sQuery(id+"F0.wireOp",EDGE,"E0.4"),sQuery(id+"F0.wireOp",EDGE,"E0.5"),subQ1,sQuery(id+"F0.wireOp",EDGE,"E0.7")])],"isStart":false})],"blendedInto":[makeQuery(id+"F1.opExtrude","CAP_FACE",FACE,{"disambiguationData":[OSD([sQuery(id+"F0.wireOp",EDGE,"E0.0"),sQuery(id+"F0.wireOp",EDGE,"E0.1"),sQuery(id+"F0.wireOp",EDGE,"E0.2"),sQuery(id+"F0.wireOp",EDGE,"E0.3"),sQuery(id+"F0.wireOp",EDGE,"E0.4"),sQuery(id+"F0.wireOp",EDGE,"E0.5"),subQ1,sQuery(id+"F0.wireOp",EDGE,"E0.7")])],"isStart":false})]});var subQ3=makeQuery(id+"F33.imprint","INTERSECT",VERTEX,{"disambiguationData":[OD(0.0)],"derivedFrom":[subQ2,subQ0]});Q5=makeQuery(id+"F33.imprint","IMPRINT",FACE,{"disambiguationData":[TD([[makeQuery(id+"F33.imprint","IMPRINT",EDGE,{"disambiguationData":[TD([[subQ3,1.0]])],"derivedFrom":subQ0}),1.0]])]});}
            var Q6;
            {var subQ0=sQuery(id+"F33.wireOp",EDGE,"E57.MirrorC");var subQ1=sQuery(id+"F0.wireOp",EDGE,"E0.6");var subQ2=makeQuery(id+"F25.opFillet","BLEND_EDGE",EDGE,{"blendedFrom":[makeQuery(id+"F1.opExtrude","CAP_EDGE",EDGE,{"disambiguationData":[OSD([subQ1])],"isStart":false}),makeQuery(id+"F1.opExtrude","CAP_FACE",FACE,{"disambiguationData":[OSD([sQuery(id+"F0.wireOp",EDGE,"E0.0"),sQuery(id+"F0.wireOp",EDGE,"E0.1"),sQuery(id+"F0.wireOp",EDGE,"E0.2"),sQuery(id+"F0.wireOp",EDGE,"E0.3"),sQuery(id+"F0.wireOp",EDGE,"E0.4"),sQuery(id+"F0.wireOp",EDGE,"E0.5"),subQ1,sQuery(id+"F0.wireOp",EDGE,"E0.7")])],"isStart":false})],"blendedInto":[makeQuery(id+"F1.opExtrude","CAP_FACE",FACE,{"disambiguationData":[OSD([sQuery(id+"F0.wireOp",EDGE,"E0.0"),sQuery(id+"F0.wireOp",EDGE,"E0.1"),sQuery(id+"F0.wireOp",EDGE,"E0.2"),sQuery(id+"F0.wireOp",EDGE,"E0.3"),sQuery(id+"F0.wireOp",EDGE,"E0.4"),sQuery(id+"F0.wireOp",EDGE,"E0.5"),subQ1,sQuery(id+"F0.wireOp",EDGE,"E0.7")])],"isStart":false})]});var subQ3=makeQuery(id+"F33.imprint","INTERSECT",VERTEX,{"disambiguationData":[OD(0.0)],"derivedFrom":[subQ2,subQ0]});Q6=makeQuery(id+"F33.imprint","IMPRINT",FACE,{"disambiguationData":[TD([[makeQuery(id+"F33.imprint","IMPRINT",EDGE,{"disambiguationData":[TD([[subQ3,1.0]])],"derivedFrom":subQ0}),1.0]])]});}
            var Q7;
            {var subQ0=sQuery(id+"F33.wireOp",EDGE,"E57.MirrorC");var subQ1=sQuery(id+"F0.wireOp",EDGE,"E0.6");var subQ2=makeQuery(id+"F25.opFillet","BLEND_EDGE",EDGE,{"blendedFrom":[makeQuery(id+"F1.opExtrude","CAP_EDGE",EDGE,{"disambiguationData":[OSD([subQ1])],"isStart":false}),makeQuery(id+"F1.opExtrude","CAP_FACE",FACE,{"disambiguationData":[OSD([sQuery(id+"F0.wireOp",EDGE,"E0.0"),sQuery(id+"F0.wireOp",EDGE,"E0.1"),sQuery(id+"F0.wireOp",EDGE,"E0.2"),sQuery(id+"F0.wireOp",EDGE,"E0.3"),sQuery(id+"F0.wireOp",EDGE,"E0.4"),sQuery(id+"F0.wireOp",EDGE,"E0.5"),subQ1,sQuery(id+"F0.wireOp",EDGE,"E0.7")])],"isStart":false})],"blendedInto":[makeQuery(id+"F1.opExtrude","CAP_FACE",FACE,{"disambiguationData":[OSD([sQuery(id+"F0.wireOp",EDGE,"E0.0"),sQuery(id+"F0.wireOp",EDGE,"E0.1"),sQuery(id+"F0.wireOp",EDGE,"E0.2"),sQuery(id+"F0.wireOp",EDGE,"E0.3"),sQuery(id+"F0.wireOp",EDGE,"E0.4"),sQuery(id+"F0.wireOp",EDGE,"E0.5"),subQ1,sQuery(id+"F0.wireOp",EDGE,"E0.7")])],"isStart":false})]});var subQ3=makeQuery(id+"F33.imprint","INTERSECT",VERTEX,{"disambiguationData":[OD(0.0)],"derivedFrom":[subQ2,subQ0]});Q7=makeQuery(id+"F33.imprint","IMPRINT",FACE,{"disambiguationData":[TD([[makeQuery(id+"F33.imprint","IMPRINT",EDGE,{"disambiguationData":[TD([[subQ3,-1.0]])],"derivedFrom":subQ0}),1.0]])]});}
            var Q8;
            {var subQ0=sQuery(id+"F33.wireOp",EDGE,"E60.MirrorC");var subQ1=sQuery(id+"F0.wireOp",EDGE,"E0.0");var subQ2=makeQuery(id+"F25.opFillet","BLEND_EDGE",EDGE,{"blendedFrom":[makeQuery(id+"F1.opExtrude","CAP_EDGE",EDGE,{"disambiguationData":[OSD([subQ1])],"isStart":false}),makeQuery(id+"F1.opExtrude","CAP_FACE",FACE,{"disambiguationData":[OSD([subQ1,sQuery(id+"F0.wireOp",EDGE,"E0.1"),sQuery(id+"F0.wireOp",EDGE,"E0.2"),sQuery(id+"F0.wireOp",EDGE,"E0.3"),sQuery(id+"F0.wireOp",EDGE,"E0.4"),sQuery(id+"F0.wireOp",EDGE,"E0.5"),sQuery(id+"F0.wireOp",EDGE,"E0.6"),sQuery(id+"F0.wireOp",EDGE,"E0.7")])],"isStart":false})],"blendedInto":[makeQuery(id+"F1.opExtrude","CAP_FACE",FACE,{"disambiguationData":[OSD([subQ1,sQuery(id+"F0.wireOp",EDGE,"E0.1"),sQuery(id+"F0.wireOp",EDGE,"E0.2"),sQuery(id+"F0.wireOp",EDGE,"E0.3"),sQuery(id+"F0.wireOp",EDGE,"E0.4"),sQuery(id+"F0.wireOp",EDGE,"E0.5"),sQuery(id+"F0.wireOp",EDGE,"E0.6"),sQuery(id+"F0.wireOp",EDGE,"E0.7")])],"isStart":false})]});var subQ3=makeQuery(id+"F33.imprint","INTERSECT",VERTEX,{"disambiguationData":[OD(0.0)],"derivedFrom":[subQ2,subQ0]});Q8=makeQuery(id+"F33.imprint","IMPRINT",FACE,{"disambiguationData":[TD([[makeQuery(id+"F33.imprint","IMPRINT",EDGE,{"disambiguationData":[TD([[subQ3,1.0]])],"derivedFrom":subQ0}),1.0]])]});}
            var Q9;
            {var subQ0=sQuery(id+"F33.wireOp",EDGE,"E60.MirrorC");var subQ1=sQuery(id+"F0.wireOp",EDGE,"E0.0");var subQ2=makeQuery(id+"F25.opFillet","BLEND_EDGE",EDGE,{"blendedFrom":[makeQuery(id+"F1.opExtrude","CAP_EDGE",EDGE,{"disambiguationData":[OSD([subQ1])],"isStart":false}),makeQuery(id+"F1.opExtrude","CAP_FACE",FACE,{"disambiguationData":[OSD([subQ1,sQuery(id+"F0.wireOp",EDGE,"E0.1"),sQuery(id+"F0.wireOp",EDGE,"E0.2"),sQuery(id+"F0.wireOp",EDGE,"E0.3"),sQuery(id+"F0.wireOp",EDGE,"E0.4"),sQuery(id+"F0.wireOp",EDGE,"E0.5"),sQuery(id+"F0.wireOp",EDGE,"E0.6"),sQuery(id+"F0.wireOp",EDGE,"E0.7")])],"isStart":false})],"blendedInto":[makeQuery(id+"F1.opExtrude","CAP_FACE",FACE,{"disambiguationData":[OSD([subQ1,sQuery(id+"F0.wireOp",EDGE,"E0.1"),sQuery(id+"F0.wireOp",EDGE,"E0.2"),sQuery(id+"F0.wireOp",EDGE,"E0.3"),sQuery(id+"F0.wireOp",EDGE,"E0.4"),sQuery(id+"F0.wireOp",EDGE,"E0.5"),sQuery(id+"F0.wireOp",EDGE,"E0.6"),sQuery(id+"F0.wireOp",EDGE,"E0.7")])],"isStart":false})]});var subQ3=makeQuery(id+"F33.imprint","INTERSECT",VERTEX,{"disambiguationData":[OD(0.0)],"derivedFrom":[subQ2,subQ0]});Q9=makeQuery(id+"F33.imprint","IMPRINT",FACE,{"disambiguationData":[TD([[makeQuery(id+"F33.imprint","IMPRINT",EDGE,{"disambiguationData":[TD([[subQ3,-1.0]])],"derivedFrom":subQ0}),1.0]])]});}
            var Q10;
            {var subQ0=sQuery(id+"F33.wireOp",EDGE,"E61.MirrorC");var subQ1=sQuery(id+"F0.wireOp",EDGE,"E0.0");var subQ2=makeQuery(id+"F25.opFillet","BLEND_EDGE",EDGE,{"blendedFrom":[makeQuery(id+"F1.opExtrude","CAP_EDGE",EDGE,{"disambiguationData":[OSD([subQ1])],"isStart":false}),makeQuery(id+"F1.opExtrude","CAP_FACE",FACE,{"disambiguationData":[OSD([subQ1,sQuery(id+"F0.wireOp",EDGE,"E0.1"),sQuery(id+"F0.wireOp",EDGE,"E0.2"),sQuery(id+"F0.wireOp",EDGE,"E0.3"),sQuery(id+"F0.wireOp",EDGE,"E0.4"),sQuery(id+"F0.wireOp",EDGE,"E0.5"),sQuery(id+"F0.wireOp",EDGE,"E0.6"),sQuery(id+"F0.wireOp",EDGE,"E0.7")])],"isStart":false})],"blendedInto":[makeQuery(id+"F1.opExtrude","CAP_FACE",FACE,{"disambiguationData":[OSD([subQ1,sQuery(id+"F0.wireOp",EDGE,"E0.1"),sQuery(id+"F0.wireOp",EDGE,"E0.2"),sQuery(id+"F0.wireOp",EDGE,"E0.3"),sQuery(id+"F0.wireOp",EDGE,"E0.4"),sQuery(id+"F0.wireOp",EDGE,"E0.5"),sQuery(id+"F0.wireOp",EDGE,"E0.6"),sQuery(id+"F0.wireOp",EDGE,"E0.7")])],"isStart":false})]});var subQ3=makeQuery(id+"F33.imprint","INTERSECT",VERTEX,{"disambiguationData":[OD(0.0)],"derivedFrom":[subQ2,subQ0]});Q10=makeQuery(id+"F33.imprint","IMPRINT",FACE,{"disambiguationData":[TD([[makeQuery(id+"F33.imprint","IMPRINT",EDGE,{"disambiguationData":[TD([[subQ3,1.0]])],"derivedFrom":subQ0}),1.0]])]});}
            var Q11;
            {var subQ0=sQuery(id+"F33.wireOp",EDGE,"E61.MirrorC");var subQ1=sQuery(id+"F0.wireOp",EDGE,"E0.0");var subQ2=makeQuery(id+"F25.opFillet","BLEND_EDGE",EDGE,{"blendedFrom":[makeQuery(id+"F1.opExtrude","CAP_EDGE",EDGE,{"disambiguationData":[OSD([subQ1])],"isStart":false}),makeQuery(id+"F1.opExtrude","CAP_FACE",FACE,{"disambiguationData":[OSD([subQ1,sQuery(id+"F0.wireOp",EDGE,"E0.1"),sQuery(id+"F0.wireOp",EDGE,"E0.2"),sQuery(id+"F0.wireOp",EDGE,"E0.3"),sQuery(id+"F0.wireOp",EDGE,"E0.4"),sQuery(id+"F0.wireOp",EDGE,"E0.5"),sQuery(id+"F0.wireOp",EDGE,"E0.6"),sQuery(id+"F0.wireOp",EDGE,"E0.7")])],"isStart":false})],"blendedInto":[makeQuery(id+"F1.opExtrude","CAP_FACE",FACE,{"disambiguationData":[OSD([subQ1,sQuery(id+"F0.wireOp",EDGE,"E0.1"),sQuery(id+"F0.wireOp",EDGE,"E0.2"),sQuery(id+"F0.wireOp",EDGE,"E0.3"),sQuery(id+"F0.wireOp",EDGE,"E0.4"),sQuery(id+"F0.wireOp",EDGE,"E0.5"),sQuery(id+"F0.wireOp",EDGE,"E0.6"),sQuery(id+"F0.wireOp",EDGE,"E0.7")])],"isStart":false})]});var subQ3=makeQuery(id+"F33.imprint","INTERSECT",VERTEX,{"disambiguationData":[OD(0.0)],"derivedFrom":[subQ2,subQ0]});Q11=makeQuery(id+"F33.imprint","IMPRINT",FACE,{"disambiguationData":[TD([[makeQuery(id+"F33.imprint","IMPRINT",EDGE,{"disambiguationData":[TD([[subQ3,-1.0]])],"derivedFrom":subQ0}),1.0]])]});}
            var Q12;
            {var subQ0=sQuery(id+"F33.wireOp",EDGE,"E55");var subQ1=sQuery(id+"F0.wireOp",EDGE,"E0.2");var subQ2=makeQuery(id+"F25.opFillet","BLEND_EDGE",EDGE,{"blendedFrom":[makeQuery(id+"F1.opExtrude","CAP_EDGE",EDGE,{"disambiguationData":[OSD([subQ1])],"isStart":false}),makeQuery(id+"F1.opExtrude","CAP_FACE",FACE,{"disambiguationData":[OSD([sQuery(id+"F0.wireOp",EDGE,"E0.0"),sQuery(id+"F0.wireOp",EDGE,"E0.1"),subQ1,sQuery(id+"F0.wireOp",EDGE,"E0.3"),sQuery(id+"F0.wireOp",EDGE,"E0.4"),sQuery(id+"F0.wireOp",EDGE,"E0.5"),sQuery(id+"F0.wireOp",EDGE,"E0.6"),sQuery(id+"F0.wireOp",EDGE,"E0.7")])],"isStart":false})],"blendedInto":[makeQuery(id+"F1.opExtrude","CAP_FACE",FACE,{"disambiguationData":[OSD([sQuery(id+"F0.wireOp",EDGE,"E0.0"),sQuery(id+"F0.wireOp",EDGE,"E0.1"),subQ1,sQuery(id+"F0.wireOp",EDGE,"E0.3"),sQuery(id+"F0.wireOp",EDGE,"E0.4"),sQuery(id+"F0.wireOp",EDGE,"E0.5"),sQuery(id+"F0.wireOp",EDGE,"E0.6"),sQuery(id+"F0.wireOp",EDGE,"E0.7")])],"isStart":false})]});var subQ3=makeQuery(id+"F33.imprint","INTERSECT",VERTEX,{"disambiguationData":[OD(0.0)],"derivedFrom":[subQ2,subQ0]});Q12=makeQuery(id+"F33.imprint","IMPRINT",FACE,{"disambiguationData":[TD([[makeQuery(id+"F33.imprint","IMPRINT",EDGE,{"disambiguationData":[TD([[subQ3,-1.0]])],"derivedFrom":subQ0}),-1.0]])]});}
            var Q13;
            {var subQ0=sQuery(id+"F33.wireOp",EDGE,"E55");var subQ1=sQuery(id+"F0.wireOp",EDGE,"E0.2");var subQ2=makeQuery(id+"F25.opFillet","BLEND_EDGE",EDGE,{"blendedFrom":[makeQuery(id+"F1.opExtrude","CAP_EDGE",EDGE,{"disambiguationData":[OSD([subQ1])],"isStart":false}),makeQuery(id+"F1.opExtrude","CAP_FACE",FACE,{"disambiguationData":[OSD([sQuery(id+"F0.wireOp",EDGE,"E0.0"),sQuery(id+"F0.wireOp",EDGE,"E0.1"),subQ1,sQuery(id+"F0.wireOp",EDGE,"E0.3"),sQuery(id+"F0.wireOp",EDGE,"E0.4"),sQuery(id+"F0.wireOp",EDGE,"E0.5"),sQuery(id+"F0.wireOp",EDGE,"E0.6"),sQuery(id+"F0.wireOp",EDGE,"E0.7")])],"isStart":false})],"blendedInto":[makeQuery(id+"F1.opExtrude","CAP_FACE",FACE,{"disambiguationData":[OSD([sQuery(id+"F0.wireOp",EDGE,"E0.0"),sQuery(id+"F0.wireOp",EDGE,"E0.1"),subQ1,sQuery(id+"F0.wireOp",EDGE,"E0.3"),sQuery(id+"F0.wireOp",EDGE,"E0.4"),sQuery(id+"F0.wireOp",EDGE,"E0.5"),sQuery(id+"F0.wireOp",EDGE,"E0.6"),sQuery(id+"F0.wireOp",EDGE,"E0.7")])],"isStart":false})]});var subQ3=makeQuery(id+"F33.imprint","INTERSECT",VERTEX,{"disambiguationData":[OD(0.0)],"derivedFrom":[subQ2,subQ0]});Q13=makeQuery(id+"F33.imprint","IMPRINT",FACE,{"disambiguationData":[TD([[makeQuery(id+"F33.imprint","IMPRINT",EDGE,{"disambiguationData":[TD([[subQ3,1.0]])],"derivedFrom":subQ0}),-1.0]])]});}
            var Q14;
            {var subQ0=sQuery(id+"F33.wireOp",EDGE,"E54");var subQ1=sQuery(id+"F0.wireOp",EDGE,"E0.2");var subQ2=makeQuery(id+"F25.opFillet","BLEND_EDGE",EDGE,{"blendedFrom":[makeQuery(id+"F1.opExtrude","CAP_EDGE",EDGE,{"disambiguationData":[OSD([subQ1])],"isStart":false}),makeQuery(id+"F1.opExtrude","CAP_FACE",FACE,{"disambiguationData":[OSD([sQuery(id+"F0.wireOp",EDGE,"E0.0"),sQuery(id+"F0.wireOp",EDGE,"E0.1"),subQ1,sQuery(id+"F0.wireOp",EDGE,"E0.3"),sQuery(id+"F0.wireOp",EDGE,"E0.4"),sQuery(id+"F0.wireOp",EDGE,"E0.5"),sQuery(id+"F0.wireOp",EDGE,"E0.6"),sQuery(id+"F0.wireOp",EDGE,"E0.7")])],"isStart":false})],"blendedInto":[makeQuery(id+"F1.opExtrude","CAP_FACE",FACE,{"disambiguationData":[OSD([sQuery(id+"F0.wireOp",EDGE,"E0.0"),sQuery(id+"F0.wireOp",EDGE,"E0.1"),subQ1,sQuery(id+"F0.wireOp",EDGE,"E0.3"),sQuery(id+"F0.wireOp",EDGE,"E0.4"),sQuery(id+"F0.wireOp",EDGE,"E0.5"),sQuery(id+"F0.wireOp",EDGE,"E0.6"),sQuery(id+"F0.wireOp",EDGE,"E0.7")])],"isStart":false})]});var subQ3=makeQuery(id+"F33.imprint","INTERSECT",VERTEX,{"disambiguationData":[OD(0.0)],"derivedFrom":[subQ2,subQ0]});Q14=makeQuery(id+"F33.imprint","IMPRINT",FACE,{"disambiguationData":[TD([[makeQuery(id+"F33.imprint","IMPRINT",EDGE,{"disambiguationData":[TD([[subQ3,1.0]])],"derivedFrom":subQ0}),-1.0]])]});}
            var Q15;
            {var subQ0=sQuery(id+"F33.wireOp",EDGE,"E54");var subQ1=sQuery(id+"F0.wireOp",EDGE,"E0.2");var subQ2=makeQuery(id+"F25.opFillet","BLEND_EDGE",EDGE,{"blendedFrom":[makeQuery(id+"F1.opExtrude","CAP_EDGE",EDGE,{"disambiguationData":[OSD([subQ1])],"isStart":false}),makeQuery(id+"F1.opExtrude","CAP_FACE",FACE,{"disambiguationData":[OSD([sQuery(id+"F0.wireOp",EDGE,"E0.0"),sQuery(id+"F0.wireOp",EDGE,"E0.1"),subQ1,sQuery(id+"F0.wireOp",EDGE,"E0.3"),sQuery(id+"F0.wireOp",EDGE,"E0.4"),sQuery(id+"F0.wireOp",EDGE,"E0.5"),sQuery(id+"F0.wireOp",EDGE,"E0.6"),sQuery(id+"F0.wireOp",EDGE,"E0.7")])],"isStart":false})],"blendedInto":[makeQuery(id+"F1.opExtrude","CAP_FACE",FACE,{"disambiguationData":[OSD([sQuery(id+"F0.wireOp",EDGE,"E0.0"),sQuery(id+"F0.wireOp",EDGE,"E0.1"),subQ1,sQuery(id+"F0.wireOp",EDGE,"E0.3"),sQuery(id+"F0.wireOp",EDGE,"E0.4"),sQuery(id+"F0.wireOp",EDGE,"E0.5"),sQuery(id+"F0.wireOp",EDGE,"E0.6"),sQuery(id+"F0.wireOp",EDGE,"E0.7")])],"isStart":false})]});var subQ3=makeQuery(id+"F33.imprint","INTERSECT",VERTEX,{"disambiguationData":[OD(0.0)],"derivedFrom":[subQ2,subQ0]});Q15=makeQuery(id+"F33.imprint","IMPRINT",FACE,{"disambiguationData":[TD([[makeQuery(id+"F33.imprint","IMPRINT",EDGE,{"disambiguationData":[TD([[subQ3,-1.0]])],"derivedFrom":subQ0}),-1.0]])]});}
            extrude(context, id + "F35", {"entities" : qUnion([Q0, Q1, Q2, Q3, Q4, Q5, Q6, Q7, Q8, Q9, Q10, Q11, Q12, Q13, Q14, Q15]), "operationType" : NewBodyOperationType.REMOVE, "oppositeDirection" : true, "depth" : 2.5 * mm});
        }
        {
            var Q0;
            Q0=makeQuery(id+"F31.imprint","IMPRINT",FACE,{"disambiguationData":[TD([[makeQuery(id+"F31.imprint","IMPRINT",EDGE,{"derivedFrom":sQuery(id+"F31.wireOp",EDGE,"E53")}),1.0]])]});
            var Q1;
            Q1=makeQuery(id+"F31.imprint","IMPRINT",FACE,{"disambiguationData":[TD([[makeQuery(id+"F31.imprint","IMPRINT",EDGE,{"derivedFrom":sQuery(id+"F31.wireOp",EDGE,"E52")}),1.0]])]});
            extrude(context, id + "F36", {"entities" : qUnion([Q0, Q1]), "operationType" : NewBodyOperationType.ADD, "depth" : 15 * mm});
        }
        {
            var Q0;
            {var subQ4=sQuery(id+"F28.wireOp",EDGE,"E45.1");Q0=makeQuery(id+"F28.imprint","IMPRINT",FACE,{"disambiguationData":[TD([[makeQuery(id+"F28.imprint","IMPRINT",EDGE,{"derivedFrom":subQ4}),1.0]])]});}
            extrude(context, id + "F37", {"entities" : qUnion([Q0]), "operationType" : NewBodyOperationType.REMOVE, "oppositeDirection" : true, "depth" : 35 * mm});
        }
        {
            var Q0;
            Q0=makeQuery(id+"F37.boolean.opBoolean","COPY",EDGE,{"derivedFrom":makeQuery(id+"F37.opExtrude","SWEPT_EDGE",EDGE,{"disambiguationData":[OSD([sQuery(id+"F28.wireOp",EDGE,"E45.4"),sQuery(id+"F28.wireOp",EDGE,"E45.15")])]})});
            var Q1;
            Q1=makeQuery(id+"F37.boolean.opBoolean","COPY",EDGE,{"derivedFrom":makeQuery(id+"F37.opExtrude","SWEPT_EDGE",EDGE,{"disambiguationData":[OSD([sQuery(id+"F28.wireOp",EDGE,"E45.1"),sQuery(id+"F28.wireOp",EDGE,"E45.2")])]})});
            var Q2;
            Q2=makeQuery(id+"F37.boolean.opBoolean","COPY",EDGE,{"derivedFrom":makeQuery(id+"F37.opExtrude","SWEPT_EDGE",EDGE,{"disambiguationData":[OSD([sQuery(id+"F28.wireOp",EDGE,"E45.13"),sQuery(id+"F28.wireOp",EDGE,"E45.15")])]})});
            var Q3;
            Q3=makeQuery(id+"F37.boolean.opBoolean","COPY",EDGE,{"derivedFrom":makeQuery(id+"F37.opExtrude","SWEPT_EDGE",EDGE,{"disambiguationData":[OSD([sQuery(id+"F28.wireOp",EDGE,"E45.0"),sQuery(id+"F28.wireOp",EDGE,"E45.1")])]})});
            var Q4;
            Q4=makeQuery(id+"F37.boolean.opBoolean","COPY",EDGE,{"derivedFrom":makeQuery(id+"F37.opExtrude","SWEPT_EDGE",EDGE,{"disambiguationData":[OSD([sQuery(id+"F28.wireOp",EDGE,"E45.9"),sQuery(id+"F28.wireOp",EDGE,"E45.10")])]})});
            var Q5;
            Q5=makeQuery(id+"F37.boolean.opBoolean","COPY",EDGE,{"derivedFrom":makeQuery(id+"F37.opExtrude","SWEPT_EDGE",EDGE,{"disambiguationData":[OSD([sQuery(id+"F28.wireOp",EDGE,"E45.6"),sQuery(id+"F28.wireOp",EDGE,"E45.7")])]})});
            var Q6;
            Q6=makeQuery(id+"F37.boolean.opBoolean","COPY",EDGE,{"derivedFrom":makeQuery(id+"F37.opExtrude","SWEPT_EDGE",EDGE,{"disambiguationData":[OSD([sQuery(id+"F28.wireOp",EDGE,"E45.10"),sQuery(id+"F28.wireOp",EDGE,"E45.11")])]})});
            var Q7;
            Q7=makeQuery(id+"F37.boolean.opBoolean","COPY",EDGE,{"derivedFrom":makeQuery(id+"F37.opExtrude","SWEPT_EDGE",EDGE,{"disambiguationData":[OSD([sQuery(id+"F28.wireOp",EDGE,"E45.7"),sQuery(id+"F28.wireOp",EDGE,"E45.8")])]})});
            fillet(context, id + "F38", {"entities" : qUnion([Q0, Q1, Q2, Q3, Q4, Q5, Q6, Q7]), "radius" : 2.5 * mm, "tangentPropagation" : true, "allowEdgeOverflow" : false});
        }
        {
            var Q0;
            Q0=makeQuery(id+"F27.boolean.opBoolean","SPLIT",BODY,{"disambiguationData":[OD(1.0)],"derivedFrom":makeQuery(id+"F1.opExtrude","SWEPT_BODY",BODY,{"disambiguationData":[OSD([sQuery(id+"F0.wireOp",EDGE,"E0.0"),sQuery(id+"F0.wireOp",EDGE,"E0.1"),sQuery(id+"F0.wireOp",EDGE,"E0.2"),sQuery(id+"F0.wireOp",EDGE,"E0.3"),sQuery(id+"F0.wireOp",EDGE,"E0.4"),sQuery(id+"F0.wireOp",EDGE,"E0.5"),sQuery(id+"F0.wireOp",EDGE,"E0.6"),sQuery(id+"F0.wireOp",EDGE,"E0.7")])]})});
            var Q1;
            Q1=makeQuery(id+"F27.boolean.opBoolean","SPLIT",BODY,{"disambiguationData":[OD(0.0)],"derivedFrom":makeQuery(id+"F1.opExtrude","SWEPT_BODY",BODY,{"disambiguationData":[OSD([sQuery(id+"F0.wireOp",EDGE,"E0.0"),sQuery(id+"F0.wireOp",EDGE,"E0.1"),sQuery(id+"F0.wireOp",EDGE,"E0.2"),sQuery(id+"F0.wireOp",EDGE,"E0.3"),sQuery(id+"F0.wireOp",EDGE,"E0.4"),sQuery(id+"F0.wireOp",EDGE,"E0.5"),sQuery(id+"F0.wireOp",EDGE,"E0.6"),sQuery(id+"F0.wireOp",EDGE,"E0.7")])]})});
            var Q2;
            Q2=makeQuery(id+"F1.opExtrude","CAP_FACE",FACE,{"disambiguationData":[OSD([sQuery(id+"F0.wireOp",EDGE,"E0.0"),sQuery(id+"F0.wireOp",EDGE,"E0.1"),sQuery(id+"F0.wireOp",EDGE,"E0.2"),sQuery(id+"F0.wireOp",EDGE,"E0.3"),sQuery(id+"F0.wireOp",EDGE,"E0.4"),sQuery(id+"F0.wireOp",EDGE,"E0.5"),sQuery(id+"F0.wireOp",EDGE,"E0.6"),sQuery(id+"F0.wireOp",EDGE,"E0.7")])],"isStart":false});
            mirror(context, id + "F39", {"entities" : qUnion([Q0, Q1]), "mirrorPlane" : qUnion([Q2])});
        }
    });
